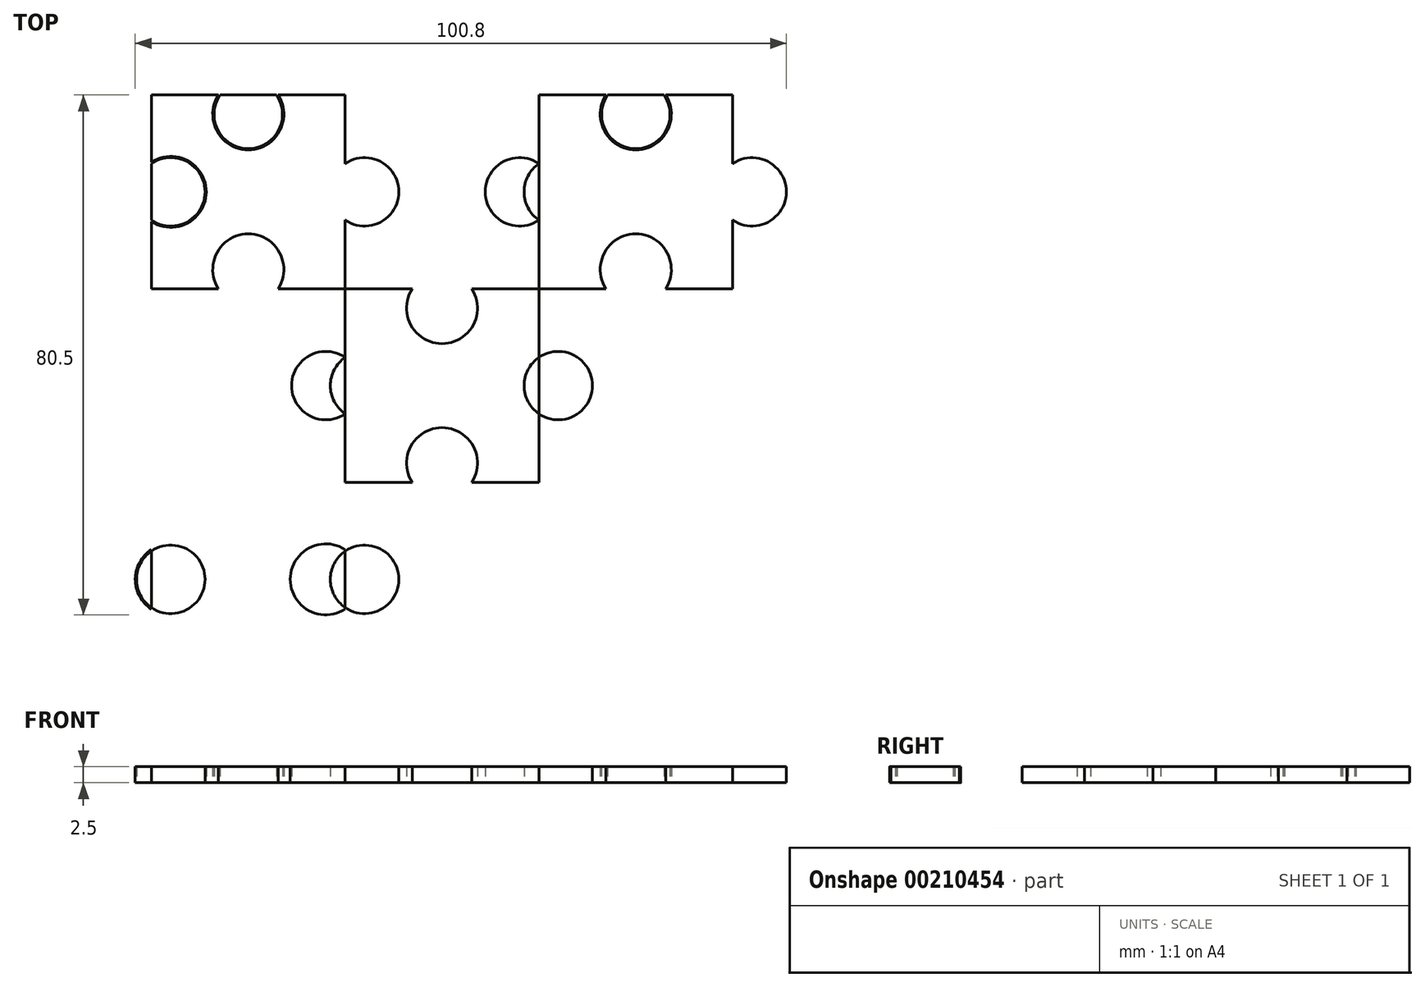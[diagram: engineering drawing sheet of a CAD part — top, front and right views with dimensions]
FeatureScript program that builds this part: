
annotation { "Feature Type Name" : "Feature", "Feature Type Description" : "" }
export const myFeature = defineFeature(function(context is Context, id is Id, definition is map)
    precondition{}
    {
        {
            var Q0;
            Q0=qCreatedBy(makeId("Top.planeOp"),FACE);
            var sketch = newSketch(context, id + "F0", { "sketchPlane" : qUnion([Q0])});
            skLineSegment(sketch, "E0.bottom", {"start": v(15, 15) * mm, "end": v(-15, 15) * mm});
            skLineSegment(sketch, "E0.top", {"start": v(15, -15) * mm, "end": v(-15, -15) * mm});
            skLineSegment(sketch, "E0.left", {"start": v(15, 15) * mm, "end": v(15, -15) * mm});
            skLineSegment(sketch, "E0.right", {"start": v(-15, 15) * mm, "end": v(-15, -15) * mm});
            skPoint(sketch, "E0.middle", {"position": v(0, 0) * mm});
            skPoint(sketch, "E1", {"position": v(0, 15) * mm});
            skPoint(sketch, "E2", {"position": v(-15, 0) * mm});
            skPoint(sketch, "E3", {"position": v(0, -15) * mm});
            skLineSegment(sketch, "E4", {"start": v(-15, 12) * mm, "end": v(15, 12) * mm, "construction": true});
            skCircle(sketch, "E5", {"center": v(0, 12) * mm, "radius": 5.5 * mm});
            skLineSegment(sketch, "E6", {"start": v(-15, 0) * mm, "end": v(15, 0) * mm, "construction": true});
            skCircle(sketch, "E7", {"center": v(0, -12) * mm, "radius": 5.5 * mm});
            skLineSegment(sketch, "E8", {"start": v(-12, 15) * mm, "end": v(-12, -15) * mm, "construction": true});
            skCircle(sketch, "E9", {"center": v(-12, 0) * mm, "radius": 5.5 * mm});
            skLineSegment(sketch, "E10", {"start": v(0, 15) * mm, "end": v(0, -15) * mm, "construction": true});
            skCircle(sketch, "E11", {"center": v(12, 0) * mm, "radius": 5.5 * mm});
            skCircle(sketch, "E12", {"center": v(-12, 0) * mm, "radius": 5.3 * mm});
            skCircle(sketch, "E13", {"center": v(0, 12) * mm, "radius": 5.3 * mm});
            skCircle(sketch, "E14", {"center": v(12, 0) * mm, "radius": 5.3 * mm});
            skCircle(sketch, "E15", {"center": v(0, -12) * mm, "radius": 5.3 * mm});
            skCircle(sketch, "E16.0.1.0", {"center": v(0, -42) * mm, "radius": 5.5 * mm});
            skCircle(sketch, "E16.0.1.1", {"center": v(-12, -30) * mm, "radius": 5.5 * mm});
            skCircle(sketch, "E16.0.1.2", {"center": v(12, -30) * mm, "radius": 5.5 * mm});
            skCircle(sketch, "E16.0.1.3", {"center": v(12, -30) * mm, "radius": 5.3 * mm});
            skLineSegment(sketch, "E16.0.1.4", {"start": v(-12, -15) * mm, "end": v(-12, -45) * mm, "construction": true});
            skPoint(sketch, "E16.0.1.5", {"position": v(0, -45) * mm});
            skLineSegment(sketch, "E16.0.1.6", {"start": v(15, -45) * mm, "end": v(-15, -45) * mm});
            skLineSegment(sketch, "E16.0.1.7", {"start": v(0, -15) * mm, "end": v(0, -45) * mm, "construction": true});
            skCircle(sketch, "E16.0.1.9", {"center": v(0, -42) * mm, "radius": 5.3 * mm});
            skLineSegment(sketch, "E16.0.1.10", {"start": v(15, -15) * mm, "end": v(15, -45) * mm});
            skLineSegment(sketch, "E16.0.1.11", {"start": v(-15, -15) * mm, "end": v(-15, -45) * mm});
            skCircle(sketch, "E16.0.1.12", {"center": v(-12, -30) * mm, "radius": 5.3 * mm});
            skPoint(sketch, "E16.0.1.13", {"position": v(-15, -30) * mm});
            skLineSegment(sketch, "E16.0.1.14", {"start": v(-15, -18) * mm, "end": v(15, -18) * mm, "construction": true});
            skCircle(sketch, "E16.0.1.16", {"center": v(0, -18) * mm, "radius": 5.5 * mm});
            skPoint(sketch, "E16.0.1.17", {"position": v(0, -30) * mm});
            skLineSegment(sketch, "E16.0.1.18", {"start": v(-15, -30) * mm, "end": v(15, -30) * mm, "construction": true});
            skCircle(sketch, "E16.0.1.19", {"center": v(0, -18) * mm, "radius": 5.3 * mm});
            skCircle(sketch, "E16.1.0.0", {"center": v(30, -12) * mm, "radius": 5.5 * mm});
            skCircle(sketch, "E16.1.0.1", {"center": v(18, 0) * mm, "radius": 5.5 * mm});
            skCircle(sketch, "E16.1.0.2", {"center": v(42, 0) * mm, "radius": 5.5 * mm});
            skCircle(sketch, "E16.1.0.3", {"center": v(42, 0) * mm, "radius": 5.3 * mm});
            skLineSegment(sketch, "E16.1.0.4", {"start": v(18, 15) * mm, "end": v(18, -15) * mm, "construction": true});
            skPoint(sketch, "E16.1.0.5", {"position": v(30, -15) * mm});
            skLineSegment(sketch, "E16.1.0.6", {"start": v(45, -15) * mm, "end": v(15, -15) * mm});
            skLineSegment(sketch, "E16.1.0.7", {"start": v(30, 15) * mm, "end": v(30, -15) * mm, "construction": true});
            skLineSegment(sketch, "E16.1.0.8", {"start": v(45, 15) * mm, "end": v(15, 15) * mm});
            skCircle(sketch, "E16.1.0.9", {"center": v(30, -12) * mm, "radius": 5.3 * mm});
            skLineSegment(sketch, "E16.1.0.10", {"start": v(45, 15) * mm, "end": v(45, -15) * mm});
            skCircle(sketch, "E16.1.0.12", {"center": v(18, 0) * mm, "radius": 5.3 * mm});
            skPoint(sketch, "E16.1.0.13", {"position": v(15, 0) * mm});
            skLineSegment(sketch, "E16.1.0.14", {"start": v(15, 12) * mm, "end": v(45, 12) * mm, "construction": true});
            skPoint(sketch, "E16.1.0.15", {"position": v(30, 15) * mm});
            skCircle(sketch, "E16.1.0.16", {"center": v(30, 12) * mm, "radius": 5.5 * mm});
            skPoint(sketch, "E16.1.0.17", {"position": v(30, 0) * mm});
            skLineSegment(sketch, "E16.1.0.18", {"start": v(15, 0) * mm, "end": v(45, 0) * mm, "construction": true});
            skCircle(sketch, "E16.1.0.19", {"center": v(30, 12) * mm, "radius": 5.3 * mm});
            skCircle(sketch, "E16.1.1.0", {"center": v(30, -42) * mm, "radius": 5.5 * mm});
            skCircle(sketch, "E16.1.1.1", {"center": v(18, -30) * mm, "radius": 5.5 * mm});
            skCircle(sketch, "E16.1.1.2", {"center": v(42, -30) * mm, "radius": 5.5 * mm});
            skCircle(sketch, "E16.1.1.3", {"center": v(42, -30) * mm, "radius": 5.3 * mm});
            skLineSegment(sketch, "E16.1.1.4", {"start": v(18, -15) * mm, "end": v(18, -45) * mm, "construction": true});
            skPoint(sketch, "E16.1.1.5", {"position": v(30, -45) * mm});
            skLineSegment(sketch, "E16.1.1.6", {"start": v(45, -45) * mm, "end": v(15, -45) * mm});
            skLineSegment(sketch, "E16.1.1.7", {"start": v(30, -15) * mm, "end": v(30, -45) * mm, "construction": true});
            skLineSegment(sketch, "E16.1.1.8", {"start": v(45, -15) * mm, "end": v(15, -15) * mm});
            skCircle(sketch, "E16.1.1.9", {"center": v(30, -42) * mm, "radius": 5.3 * mm});
            skLineSegment(sketch, "E16.1.1.10", {"start": v(45, -15) * mm, "end": v(45, -45) * mm});
            skLineSegment(sketch, "E16.1.1.11", {"start": v(15, -15) * mm, "end": v(15, -45) * mm});
            skCircle(sketch, "E16.1.1.12", {"center": v(18, -30) * mm, "radius": 5.3 * mm});
            skPoint(sketch, "E16.1.1.13", {"position": v(15, -30) * mm});
            skLineSegment(sketch, "E16.1.1.14", {"start": v(15, -18) * mm, "end": v(45, -18) * mm, "construction": true});
            skPoint(sketch, "E16.1.1.15", {"position": v(30, -15) * mm});
            skCircle(sketch, "E16.1.1.16", {"center": v(30, -18) * mm, "radius": 5.5 * mm});
            skPoint(sketch, "E16.1.1.17", {"position": v(30, -30) * mm});
            skLineSegment(sketch, "E16.1.1.18", {"start": v(15, -30) * mm, "end": v(45, -30) * mm, "construction": true});
            skCircle(sketch, "E16.1.1.19", {"center": v(30, -18) * mm, "radius": 5.3 * mm});
            skCircle(sketch, "E16.2.0.0", {"center": v(60, -12) * mm, "radius": 5.5 * mm});
            skCircle(sketch, "E16.2.0.1", {"center": v(48, 0) * mm, "radius": 5.5 * mm});
            skCircle(sketch, "E16.2.0.2", {"center": v(72, 0) * mm, "radius": 5.5 * mm});
            skCircle(sketch, "E16.2.0.3", {"center": v(72, 0) * mm, "radius": 5.3 * mm});
            skLineSegment(sketch, "E16.2.0.4", {"start": v(48, 15) * mm, "end": v(48, -15) * mm, "construction": true});
            skPoint(sketch, "E16.2.0.5", {"position": v(60, -15) * mm});
            skLineSegment(sketch, "E16.2.0.6", {"start": v(75, -15) * mm, "end": v(45, -15) * mm});
            skLineSegment(sketch, "E16.2.0.7", {"start": v(60, 15) * mm, "end": v(60, -15) * mm, "construction": true});
            skLineSegment(sketch, "E16.2.0.8", {"start": v(75, 15) * mm, "end": v(45, 15) * mm});
            skCircle(sketch, "E16.2.0.9", {"center": v(60, -12) * mm, "radius": 5.3 * mm});
            skLineSegment(sketch, "E16.2.0.10", {"start": v(75, 15) * mm, "end": v(75, -15) * mm});
            skLineSegment(sketch, "E16.2.0.11", {"start": v(45, 15) * mm, "end": v(45, -15) * mm});
            skCircle(sketch, "E16.2.0.12", {"center": v(48, 0) * mm, "radius": 5.3 * mm});
            skPoint(sketch, "E16.2.0.13", {"position": v(45, 0) * mm});
            skLineSegment(sketch, "E16.2.0.14", {"start": v(45, 12) * mm, "end": v(75, 12) * mm, "construction": true});
            skPoint(sketch, "E16.2.0.15", {"position": v(60, 15) * mm});
            skCircle(sketch, "E16.2.0.16", {"center": v(60, 12) * mm, "radius": 5.5 * mm});
            skPoint(sketch, "E16.2.0.17", {"position": v(60, 0) * mm});
            skLineSegment(sketch, "E16.2.0.18", {"start": v(45, 0) * mm, "end": v(75, 0) * mm, "construction": true});
            skCircle(sketch, "E16.2.0.19", {"center": v(60, 12) * mm, "radius": 5.3 * mm});
            skCircle(sketch, "E16.2.1.0", {"center": v(60, -42) * mm, "radius": 5.5 * mm});
            skCircle(sketch, "E16.2.1.1", {"center": v(48, -30) * mm, "radius": 5.5 * mm});
            skCircle(sketch, "E16.2.1.2", {"center": v(72, -30) * mm, "radius": 5.5 * mm});
            skCircle(sketch, "E16.2.1.3", {"center": v(72, -30) * mm, "radius": 5.3 * mm});
            skLineSegment(sketch, "E16.2.1.4", {"start": v(48, -15) * mm, "end": v(48, -45) * mm, "construction": true});
            skPoint(sketch, "E16.2.1.5", {"position": v(60, -45) * mm});
            skLineSegment(sketch, "E16.2.1.6", {"start": v(75, -45) * mm, "end": v(45, -45) * mm});
            skLineSegment(sketch, "E16.2.1.7", {"start": v(60, -15) * mm, "end": v(60, -45) * mm, "construction": true});
            skLineSegment(sketch, "E16.2.1.8", {"start": v(75, -15) * mm, "end": v(45, -15) * mm});
            skCircle(sketch, "E16.2.1.9", {"center": v(60, -42) * mm, "radius": 5.3 * mm});
            skLineSegment(sketch, "E16.2.1.10", {"start": v(75, -15) * mm, "end": v(75, -45) * mm});
            skLineSegment(sketch, "E16.2.1.11", {"start": v(45, -15) * mm, "end": v(45, -45) * mm});
            skCircle(sketch, "E16.2.1.12", {"center": v(48, -30) * mm, "radius": 5.3 * mm});
            skPoint(sketch, "E16.2.1.13", {"position": v(45, -30) * mm});
            skLineSegment(sketch, "E16.2.1.14", {"start": v(45, -18) * mm, "end": v(75, -18) * mm, "construction": true});
            skPoint(sketch, "E16.2.1.15", {"position": v(60, -15) * mm});
            skCircle(sketch, "E16.2.1.16", {"center": v(60, -18) * mm, "radius": 5.5 * mm});
            skPoint(sketch, "E16.2.1.17", {"position": v(60, -30) * mm});
            skLineSegment(sketch, "E16.2.1.18", {"start": v(45, -30) * mm, "end": v(75, -30) * mm, "construction": true});
            skCircle(sketch, "E16.2.1.19", {"center": v(60, -18) * mm, "radius": 5.3 * mm});
            skLineSegment(sketch, "E16.direction1", {"start": v(-15, -15) * mm, "end": v(15, -15) * mm, "construction": true});
            skLineSegment(sketch, "E16.direction2", {"start": v(-15, -15) * mm, "end": v(-15, -45) * mm, "construction": true});
            skCircle(sketch, "E17.0.0.2", {"center": v(0, -72) * mm, "radius": 5.5 * mm});
            skCircle(sketch, "E17.2.0.2", {"center": v(-12, -60) * mm, "radius": 5.5 * mm});
            skCircle(sketch, "E17.4.0.2", {"center": v(12, -60) * mm, "radius": 5.5 * mm});
            skCircle(sketch, "E17.6.0.2", {"center": v(12, -60) * mm, "radius": 5.3 * mm});
            skLineSegment(sketch, "E17.8.0.2", {"start": v(-12, -45) * mm, "end": v(-12, -75) * mm, "construction": true});
            skPoint(sketch, "E17.11.0.2", {"position": v(0, -75) * mm});
            skLineSegment(sketch, "E17.12.0.2", {"start": v(15, -75) * mm, "end": v(-15, -75) * mm});
            skLineSegment(sketch, "E17.15.0.2", {"start": v(0, -45) * mm, "end": v(0, -75) * mm, "construction": true});
            skCircle(sketch, "E17.21.0.2", {"center": v(0, -72) * mm, "radius": 5.3 * mm});
            skLineSegment(sketch, "E17.23.0.2", {"start": v(15, -45) * mm, "end": v(15, -75) * mm});
            skLineSegment(sketch, "E17.26.0.2", {"start": v(-15, -45) * mm, "end": v(-15, -75) * mm});
            skCircle(sketch, "E17.29.0.2", {"center": v(-12, -60) * mm, "radius": 5.3 * mm});
            skPoint(sketch, "E17.31.0.2", {"position": v(-15, -60) * mm});
            skLineSegment(sketch, "E17.32.0.2", {"start": v(-15, -48) * mm, "end": v(15, -48) * mm, "construction": true});
            skCircle(sketch, "E17.36.0.2", {"center": v(0, -48) * mm, "radius": 5.5 * mm});
            skPoint(sketch, "E17.38.0.2", {"position": v(0, -60) * mm});
            skLineSegment(sketch, "E17.39.0.2", {"start": v(-15, -60) * mm, "end": v(15, -60) * mm, "construction": true});
            skCircle(sketch, "E17.42.0.2", {"center": v(0, -48) * mm, "radius": 5.3 * mm});
            skCircle(sketch, "E17.0.1.2", {"center": v(30, -72) * mm, "radius": 5.5 * mm});
            skCircle(sketch, "E17.2.1.2", {"center": v(18, -60) * mm, "radius": 5.5 * mm});
            skCircle(sketch, "E17.4.1.2", {"center": v(42, -60) * mm, "radius": 5.5 * mm});
            skCircle(sketch, "E17.6.1.2", {"center": v(42, -60) * mm, "radius": 5.3 * mm});
            skLineSegment(sketch, "E17.8.1.2", {"start": v(18, -45) * mm, "end": v(18, -75) * mm, "construction": true});
            skPoint(sketch, "E17.11.1.2", {"position": v(30, -75) * mm});
            skLineSegment(sketch, "E17.12.1.2", {"start": v(45, -75) * mm, "end": v(15, -75) * mm});
            skLineSegment(sketch, "E17.15.1.2", {"start": v(30, -45) * mm, "end": v(30, -75) * mm, "construction": true});
            skCircle(sketch, "E17.21.1.2", {"center": v(30, -72) * mm, "radius": 5.3 * mm});
            skLineSegment(sketch, "E17.23.1.2", {"start": v(45, -45) * mm, "end": v(45, -75) * mm});
            skLineSegment(sketch, "E17.26.1.2", {"start": v(15, -45) * mm, "end": v(15, -75) * mm});
            skCircle(sketch, "E17.29.1.2", {"center": v(18, -60) * mm, "radius": 5.3 * mm});
            skPoint(sketch, "E17.31.1.2", {"position": v(15, -60) * mm});
            skLineSegment(sketch, "E17.32.1.2", {"start": v(15, -48) * mm, "end": v(45, -48) * mm, "construction": true});
            skCircle(sketch, "E17.36.1.2", {"center": v(30, -48) * mm, "radius": 5.5 * mm});
            skPoint(sketch, "E17.38.1.2", {"position": v(30, -60) * mm});
            skLineSegment(sketch, "E17.39.1.2", {"start": v(15, -60) * mm, "end": v(45, -60) * mm, "construction": true});
            skCircle(sketch, "E17.42.1.2", {"center": v(30, -48) * mm, "radius": 5.3 * mm});
            skCircle(sketch, "E17.0.2.2", {"center": v(60, -72) * mm, "radius": 5.5 * mm});
            skCircle(sketch, "E17.2.2.2", {"center": v(48, -60) * mm, "radius": 5.5 * mm});
            skCircle(sketch, "E17.4.2.2", {"center": v(72, -60) * mm, "radius": 5.5 * mm});
            skCircle(sketch, "E17.6.2.2", {"center": v(72, -60) * mm, "radius": 5.3 * mm});
            skLineSegment(sketch, "E17.8.2.2", {"start": v(48, -45) * mm, "end": v(48, -75) * mm, "construction": true});
            skPoint(sketch, "E17.11.2.2", {"position": v(60, -75) * mm});
            skLineSegment(sketch, "E17.12.2.2", {"start": v(75, -75) * mm, "end": v(45, -75) * mm});
            skLineSegment(sketch, "E17.15.2.2", {"start": v(60, -45) * mm, "end": v(60, -75) * mm, "construction": true});
            skCircle(sketch, "E17.21.2.2", {"center": v(60, -72) * mm, "radius": 5.3 * mm});
            skLineSegment(sketch, "E17.23.2.2", {"start": v(75, -45) * mm, "end": v(75, -75) * mm});
            skLineSegment(sketch, "E17.26.2.2", {"start": v(45, -45) * mm, "end": v(45, -75) * mm});
            skCircle(sketch, "E17.29.2.2", {"center": v(48, -60) * mm, "radius": 5.3 * mm});
            skPoint(sketch, "E17.31.2.2", {"position": v(45, -60) * mm});
            skLineSegment(sketch, "E17.32.2.2", {"start": v(45, -48) * mm, "end": v(75, -48) * mm, "construction": true});
            skCircle(sketch, "E17.36.2.2", {"center": v(60, -48) * mm, "radius": 5.5 * mm});
            skPoint(sketch, "E17.38.2.2", {"position": v(60, -60) * mm});
            skLineSegment(sketch, "E17.39.2.2", {"start": v(45, -60) * mm, "end": v(75, -60) * mm, "construction": true});
            skCircle(sketch, "E17.42.2.2", {"center": v(60, -48) * mm, "radius": 5.3 * mm});
            skCircle(sketch, "E18.0.3.0", {"center": v(90, -12) * mm, "radius": 5.5 * mm});
            skCircle(sketch, "E18.2.3.0", {"center": v(78, 0) * mm, "radius": 5.5 * mm});
            skCircle(sketch, "E18.4.3.0", {"center": v(102, 0) * mm, "radius": 5.5 * mm});
            skCircle(sketch, "E18.6.3.0", {"center": v(102, 0) * mm, "radius": 5.3 * mm});
            skLineSegment(sketch, "E18.8.3.0", {"start": v(78, 15) * mm, "end": v(78, -15) * mm, "construction": true});
            skPoint(sketch, "E18.11.3.0", {"position": v(90, -15) * mm});
            skLineSegment(sketch, "E18.12.3.0", {"start": v(105, -15) * mm, "end": v(75, -15) * mm});
            skLineSegment(sketch, "E18.15.3.0", {"start": v(90, 15) * mm, "end": v(90, -15) * mm, "construction": true});
            skLineSegment(sketch, "E18.18.3.0", {"start": v(105, 15) * mm, "end": v(75, 15) * mm});
            skCircle(sketch, "E18.21.3.0", {"center": v(90, -12) * mm, "radius": 5.3 * mm});
            skLineSegment(sketch, "E18.23.3.0", {"start": v(105, 15) * mm, "end": v(105, -15) * mm});
            skCircle(sketch, "E18.29.3.0", {"center": v(78, 0) * mm, "radius": 5.3 * mm});
            skPoint(sketch, "E18.31.3.0", {"position": v(75, 0) * mm});
            skLineSegment(sketch, "E18.32.3.0", {"start": v(75, 12) * mm, "end": v(105, 12) * mm, "construction": true});
            skPoint(sketch, "E18.35.3.0", {"position": v(90, 15) * mm});
            skCircle(sketch, "E18.36.3.0", {"center": v(90, 12) * mm, "radius": 5.5 * mm});
            skPoint(sketch, "E18.38.3.0", {"position": v(90, 0) * mm});
            skLineSegment(sketch, "E18.39.3.0", {"start": v(75, 0) * mm, "end": v(105, 0) * mm, "construction": true});
            skCircle(sketch, "E18.42.3.0", {"center": v(90, 12) * mm, "radius": 5.3 * mm});
            skCircle(sketch, "E18.0.3.1", {"center": v(90, -42) * mm, "radius": 5.5 * mm});
            skCircle(sketch, "E18.2.3.1", {"center": v(78, -30) * mm, "radius": 5.5 * mm});
            skCircle(sketch, "E18.4.3.1", {"center": v(102, -30) * mm, "radius": 5.5 * mm});
            skCircle(sketch, "E18.6.3.1", {"center": v(102, -30) * mm, "radius": 5.3 * mm});
            skLineSegment(sketch, "E18.8.3.1", {"start": v(78, -15) * mm, "end": v(78, -45) * mm, "construction": true});
            skPoint(sketch, "E18.11.3.1", {"position": v(90, -45) * mm});
            skLineSegment(sketch, "E18.12.3.1", {"start": v(105, -45) * mm, "end": v(75, -45) * mm});
            skLineSegment(sketch, "E18.15.3.1", {"start": v(90, -15) * mm, "end": v(90, -45) * mm, "construction": true});
            skLineSegment(sketch, "E18.18.3.1", {"start": v(105, -15) * mm, "end": v(75, -15) * mm});
            skCircle(sketch, "E18.21.3.1", {"center": v(90, -42) * mm, "radius": 5.3 * mm});
            skLineSegment(sketch, "E18.23.3.1", {"start": v(105, -15) * mm, "end": v(105, -45) * mm});
            skCircle(sketch, "E18.29.3.1", {"center": v(78, -30) * mm, "radius": 5.3 * mm});
            skPoint(sketch, "E18.31.3.1", {"position": v(75, -30) * mm});
            skLineSegment(sketch, "E18.32.3.1", {"start": v(75, -18) * mm, "end": v(105, -18) * mm, "construction": true});
            skPoint(sketch, "E18.35.3.1", {"position": v(90, -15) * mm});
            skCircle(sketch, "E18.36.3.1", {"center": v(90, -18) * mm, "radius": 5.5 * mm});
            skPoint(sketch, "E18.38.3.1", {"position": v(90, -30) * mm});
            skLineSegment(sketch, "E18.39.3.1", {"start": v(75, -30) * mm, "end": v(105, -30) * mm, "construction": true});
            skCircle(sketch, "E18.42.3.1", {"center": v(90, -18) * mm, "radius": 5.3 * mm});
            skCircle(sketch, "E18.0.3.2", {"center": v(90, -72) * mm, "radius": 5.5 * mm});
            skCircle(sketch, "E18.2.3.2", {"center": v(78, -60) * mm, "radius": 5.5 * mm});
            skCircle(sketch, "E18.4.3.2", {"center": v(102, -60) * mm, "radius": 5.5 * mm});
            skCircle(sketch, "E18.6.3.2", {"center": v(102, -60) * mm, "radius": 5.3 * mm});
            skLineSegment(sketch, "E18.8.3.2", {"start": v(78, -45) * mm, "end": v(78, -75) * mm, "construction": true});
            skPoint(sketch, "E18.11.3.2", {"position": v(90, -75) * mm});
            skLineSegment(sketch, "E18.12.3.2", {"start": v(105, -75) * mm, "end": v(75, -75) * mm});
            skLineSegment(sketch, "E18.15.3.2", {"start": v(90, -45) * mm, "end": v(90, -75) * mm, "construction": true});
            skLineSegment(sketch, "E18.18.3.2", {"start": v(105, -45) * mm, "end": v(75, -45) * mm});
            skCircle(sketch, "E18.21.3.2", {"center": v(90, -72) * mm, "radius": 5.3 * mm});
            skLineSegment(sketch, "E18.23.3.2", {"start": v(105, -45) * mm, "end": v(105, -75) * mm});
            skCircle(sketch, "E18.29.3.2", {"center": v(78, -60) * mm, "radius": 5.3 * mm});
            skPoint(sketch, "E18.31.3.2", {"position": v(75, -60) * mm});
            skLineSegment(sketch, "E18.32.3.2", {"start": v(75, -48) * mm, "end": v(105, -48) * mm, "construction": true});
            skPoint(sketch, "E18.35.3.2", {"position": v(90, -45) * mm});
            skCircle(sketch, "E18.36.3.2", {"center": v(90, -48) * mm, "radius": 5.5 * mm});
            skPoint(sketch, "E18.38.3.2", {"position": v(90, -60) * mm});
            skLineSegment(sketch, "E18.39.3.2", {"start": v(75, -60) * mm, "end": v(105, -60) * mm, "construction": true});
            skCircle(sketch, "E18.42.3.2", {"center": v(90, -48) * mm, "radius": 5.3 * mm});
            skSolve(sketch);
        }
        {
            var Q0;
            {var subQ1=sQuery(id+"F0.wireOp",EDGE,"E0.right");var subQ13=sQuery(id+"F0.wireOp",EDGE,"E0.bottom");var subQ14=makeQuery(id+"F0.imprint","INTERSECT",VERTEX,{"derivedFrom":[subQ13,subQ1]});Q0=makeQuery(id+"F0.imprint","IMPRINT",FACE,{"disambiguationData":[TD([[makeQuery(id+"F0.imprint","IMPRINT",EDGE,{"disambiguationData":[TD([[subQ14,1.0]])],"derivedFrom":subQ13}),1.0]])]});}
            var Q1;
            {var subQ0=sQuery(id+"F0.wireOp",EDGE,"E5");var subQ1=sQuery(id+"F0.wireOp",EDGE,"E0.bottom");var subQ2=makeQuery(id+"F0.imprint","INTERSECT",VERTEX,{"disambiguationData":[OD(0.0)],"derivedFrom":[subQ1,subQ0]});Q1=makeQuery(id+"F0.imprint","IMPRINT",FACE,{"disambiguationData":[TD([[makeQuery(id+"F0.imprint","IMPRINT",EDGE,{"disambiguationData":[TD([[subQ2,-1.0]])],"derivedFrom":subQ1}),1.0]])]});}
            var Q2;
            {var subQ0=sQuery(id+"F0.wireOp",EDGE,"E16.1.0.12");var subQ1=sQuery(id+"F0.wireOp",EDGE,"E11");var subQ2=makeQuery(id+"F0.imprint","INTERSECT",VERTEX,{"disambiguationData":[OD(0.0)],"derivedFrom":[subQ1,subQ0]});Q2=makeQuery(id+"F0.imprint","IMPRINT",FACE,{"disambiguationData":[TD([[makeQuery(id+"F0.imprint","IMPRINT",EDGE,{"disambiguationData":[TD([[subQ2,1.0]])],"derivedFrom":subQ1}),1.0]])]});}
            var Q3;
            {var subQ0=sQuery(id+"F0.wireOp",EDGE,"E12");var subQ1=sQuery(id+"F0.wireOp",EDGE,"E0.right");var subQ2=makeQuery(id+"F0.imprint","INTERSECT",VERTEX,{"disambiguationData":[OD(0.0)],"derivedFrom":[subQ1,subQ0]});Q3=makeQuery(id+"F0.imprint","IMPRINT",FACE,{"disambiguationData":[TD([[makeQuery(id+"F0.imprint","IMPRINT",EDGE,{"disambiguationData":[TD([[subQ2,-1.0]])],"derivedFrom":subQ1}),1.0]])]});}
            var Q4;
            {var subQ0=sQuery(id+"F0.wireOp",EDGE,"E13");var subQ1=sQuery(id+"F0.wireOp",EDGE,"E0.bottom");var subQ2=makeQuery(id+"F0.imprint","INTERSECT",VERTEX,{"disambiguationData":[OD(0.0)],"derivedFrom":[subQ1,subQ0]});Q4=makeQuery(id+"F0.imprint","IMPRINT",FACE,{"disambiguationData":[TD([[makeQuery(id+"F0.imprint","IMPRINT",EDGE,{"disambiguationData":[TD([[subQ2,-1.0]])],"derivedFrom":subQ1}),1.0]])]});}
            var Q5;
            {var subQ0=sQuery(id+"F0.wireOp",EDGE,"E16.1.0.1");var subQ1=sQuery(id+"F0.wireOp",EDGE,"E14");var subQ2=makeQuery(id+"F0.imprint","INTERSECT",VERTEX,{"disambiguationData":[OD(0.0)],"derivedFrom":[subQ1,subQ0]});Q5=makeQuery(id+"F0.imprint","IMPRINT",FACE,{"disambiguationData":[TD([[makeQuery(id+"F0.imprint","IMPRINT",EDGE,{"disambiguationData":[TD([[subQ2,-1.0]])],"derivedFrom":subQ1}),1.0]])]});}
            var Q6;
            {var subQ0=sQuery(id+"F0.wireOp",EDGE,"E16.1.0.12");var subQ1=sQuery(id+"F0.wireOp",EDGE,"E0.left");var subQ2=sQuery(id+"F0.wireOp",EDGE,"E14");var subQ3=makeQuery(id+"F0.imprint","INTERSECT",VERTEX,{"disambiguationData":[OD(0.0)],"derivedFrom":[subQ2,subQ1,subQ0]});Q6=makeQuery(id+"F0.imprint","IMPRINT",FACE,{"disambiguationData":[TD([[makeQuery(id+"F0.imprint","IMPRINT",EDGE,{"disambiguationData":[TD([[subQ3,-1.0]])],"derivedFrom":subQ1}),-1.0]])]});}
            var Q7;
            {var subQ0=sQuery(id+"F0.wireOp",EDGE,"E16.1.0.12");var subQ1=sQuery(id+"F0.wireOp",EDGE,"E0.left");var subQ2=sQuery(id+"F0.wireOp",EDGE,"E14");var subQ3=makeQuery(id+"F0.imprint","INTERSECT",VERTEX,{"disambiguationData":[OD(0.0)],"derivedFrom":[subQ2,subQ1,subQ0]});Q7=makeQuery(id+"F0.imprint","IMPRINT",FACE,{"disambiguationData":[TD([[makeQuery(id+"F0.imprint","IMPRINT",EDGE,{"disambiguationData":[TD([[subQ3,1.0]])],"derivedFrom":subQ2}),1.0]])]});}
            var Q8;
            {var subQ0=sQuery(id+"F0.wireOp",EDGE,"E16.1.0.12");var subQ1=sQuery(id+"F0.wireOp",EDGE,"E11");var subQ2=makeQuery(id+"F0.imprint","INTERSECT",VERTEX,{"disambiguationData":[OD(0.0)],"derivedFrom":[subQ1,subQ0]});Q8=makeQuery(id+"F0.imprint","IMPRINT",FACE,{"disambiguationData":[TD([[makeQuery(id+"F0.imprint","IMPRINT",EDGE,{"disambiguationData":[TD([[subQ2,1.0]])],"derivedFrom":subQ1}),-1.0]])]});}
            var Q9;
            {var subQ0=sQuery(id+"F0.wireOp",EDGE,"E16.1.0.1");var subQ1=sQuery(id+"F0.wireOp",EDGE,"E14");var subQ2=makeQuery(id+"F0.imprint","INTERSECT",VERTEX,{"disambiguationData":[OD(0.0)],"derivedFrom":[subQ1,subQ0]});Q9=makeQuery(id+"F0.imprint","IMPRINT",FACE,{"disambiguationData":[TD([[makeQuery(id+"F0.imprint","IMPRINT",EDGE,{"disambiguationData":[TD([[subQ2,-1.0]])],"derivedFrom":subQ0}),1.0]])]});}
            var Q10;
            {var subQ0=sQuery(id+"F0.wireOp",EDGE,"E9");var subQ1=sQuery(id+"F0.wireOp",EDGE,"E0.right");var subQ2=makeQuery(id+"F0.imprint","INTERSECT",VERTEX,{"disambiguationData":[OD(0.0)],"derivedFrom":[subQ1,subQ0]});Q10=makeQuery(id+"F0.imprint","IMPRINT",FACE,{"disambiguationData":[TD([[makeQuery(id+"F0.imprint","IMPRINT",EDGE,{"disambiguationData":[TD([[subQ2,-1.0]])],"derivedFrom":subQ1}),1.0]])]});}
            var Q11;
            {var subQ1=sQuery(id+"F0.wireOp",EDGE,"E16.1.0.1");var subQ5=sQuery(id+"F0.wireOp",EDGE,"E14");var subQ6=makeQuery(id+"F0.imprint","INTERSECT",VERTEX,{"disambiguationData":[OD(0.0)],"derivedFrom":[subQ5,subQ1]});Q11=makeQuery(id+"F0.imprint","IMPRINT",FACE,{"disambiguationData":[TD([[makeQuery(id+"F0.imprint","IMPRINT",EDGE,{"disambiguationData":[TD([[subQ6,-1.0]])],"derivedFrom":subQ5}),-1.0]])]});}
            var Q12;
            {var subQ0=sQuery(id+"F0.wireOp",EDGE,"E16.1.0.1");var subQ1=sQuery(id+"F0.wireOp",EDGE,"E14");var subQ2=makeQuery(id+"F0.imprint","INTERSECT",VERTEX,{"disambiguationData":[OD(0.0)],"derivedFrom":[subQ1,subQ0]});Q12=makeQuery(id+"F0.imprint","IMPRINT",FACE,{"disambiguationData":[TD([[makeQuery(id+"F0.imprint","IMPRINT",EDGE,{"disambiguationData":[TD([[subQ2,1.0]])],"derivedFrom":subQ1}),-1.0]])]});}
            var Q13;
            {var subQ0=sQuery(id+"F0.wireOp",EDGE,"E16.1.0.1");var subQ1=sQuery(id+"F0.wireOp",EDGE,"E14");var subQ2=makeQuery(id+"F0.imprint","INTERSECT",VERTEX,{"disambiguationData":[OD(1.0)],"derivedFrom":[subQ1,subQ0]});Q13=makeQuery(id+"F0.imprint","IMPRINT",FACE,{"disambiguationData":[TD([[makeQuery(id+"F0.imprint","IMPRINT",EDGE,{"disambiguationData":[TD([[subQ2,-1.0]])],"derivedFrom":subQ1}),-1.0]])]});}
            extrude(context, id + "F1", {"entities" : qUnion([Q0, Q1, Q2, Q3, Q4, Q5, Q6, Q7, Q8, Q9, Q10, Q11, Q12, Q13]), "depth" : 2.5 * mm});
        }
        {
            var Q0;
            {var subQ1=sQuery(id+"F0.wireOp",EDGE,"adf34985-a7f9-4340-8066-421a328eff77.28.0.2");var subQ17=sQuery(id+"F0.wireOp",EDGE,"adf34985-a7f9-4340-8066-421a328eff77.2.0.2");var subQ19=makeQuery(id+"F0.imprint","INTERSECT",VERTEX,{"disambiguationData":[OD(0.0)],"derivedFrom":[subQ17,subQ1]});Q0=makeQuery(id+"F0.imprint","IMPRINT",FACE,{"disambiguationData":[TD([[makeQuery(id+"F0.imprint","IMPRINT",EDGE,{"disambiguationData":[TD([[subQ19,1.0]])],"derivedFrom":subQ17}),-1.0]])]});}
            var Q1;
            {var subQ0=sQuery(id+"F0.wireOp",EDGE,"adf34985-a7f9-4340-8066-421a328eff77.28.0.2");var subQ1=sQuery(id+"F0.wireOp",EDGE,"adf34985-a7f9-4340-8066-421a328eff77.2.0.2");var subQ2=makeQuery(id+"F0.imprint","INTERSECT",VERTEX,{"disambiguationData":[OD(0.0)],"derivedFrom":[subQ1,subQ0]});Q1=makeQuery(id+"F0.imprint","IMPRINT",FACE,{"disambiguationData":[TD([[makeQuery(id+"F0.imprint","IMPRINT",EDGE,{"disambiguationData":[TD([[subQ2,1.0]])],"derivedFrom":subQ1}),1.0]])]});}
            var Q2;
            {var subQ0=sQuery(id+"F0.wireOp",EDGE,"adf34985-a7f9-4340-8066-421a328eff77.28.1.2");var subQ1=sQuery(id+"F0.wireOp",EDGE,"adf34985-a7f9-4340-8066-421a328eff77.2.1.2");var subQ2=sQuery(id+"F0.wireOp",EDGE,"adf34985-a7f9-4340-8066-421a328eff77.4.0.2");var subQ3=makeQuery(id+"F0.imprint","INTERSECT",VERTEX,{"disambiguationData":[OD(0.0)],"derivedFrom":[subQ2,subQ1,subQ0]});Q2=makeQuery(id+"F0.imprint","IMPRINT",FACE,{"disambiguationData":[TD([[makeQuery(id+"F0.imprint","IMPRINT",EDGE,{"disambiguationData":[TD([[subQ3,-1.0]])],"derivedFrom":subQ2}),1.0]])]});}
            var Q3;
            {var subQ0=sQuery(id+"F0.wireOp",EDGE,"adf34985-a7f9-4340-8066-421a328eff77.28.1.2");var subQ1=sQuery(id+"F0.wireOp",EDGE,"adf34985-a7f9-4340-8066-421a328eff77.2.1.2");var subQ2=sQuery(id+"F0.wireOp",EDGE,"adf34985-a7f9-4340-8066-421a328eff77.4.0.2");var subQ3=makeQuery(id+"F0.imprint","INTERSECT",VERTEX,{"disambiguationData":[OD(0.0)],"derivedFrom":[subQ2,subQ1,subQ0]});Q3=makeQuery(id+"F0.imprint","IMPRINT",FACE,{"disambiguationData":[TD([[makeQuery(id+"F0.imprint","IMPRINT",EDGE,{"disambiguationData":[TD([[subQ3,1.0]])],"derivedFrom":subQ2}),-1.0]])]});}
            var Q4;
            {var subQ0=sQuery(id+"F0.wireOp",EDGE,"adf34985-a7f9-4340-8066-421a328eff77.28.1.2");var subQ1=sQuery(id+"F0.wireOp",EDGE,"adf34985-a7f9-4340-8066-421a328eff77.2.1.2");var subQ2=sQuery(id+"F0.wireOp",EDGE,"adf34985-a7f9-4340-8066-421a328eff77.4.0.2");var subQ3=makeQuery(id+"F0.imprint","INTERSECT",VERTEX,{"disambiguationData":[OD(0.0)],"derivedFrom":[subQ2,subQ1,subQ0]});Q4=makeQuery(id+"F0.imprint","IMPRINT",FACE,{"disambiguationData":[TD([[makeQuery(id+"F0.imprint","IMPRINT",EDGE,{"disambiguationData":[TD([[subQ3,1.0]])],"derivedFrom":subQ2}),1.0]])]});}
            var Q5;
            {var subQ0=sQuery(id+"F0.wireOp",EDGE,"adf34985-a7f9-4340-8066-421a328eff77.28.1.2");var subQ1=sQuery(id+"F0.wireOp",EDGE,"adf34985-a7f9-4340-8066-421a328eff77.2.1.2");var subQ2=sQuery(id+"F0.wireOp",EDGE,"adf34985-a7f9-4340-8066-421a328eff77.4.0.2");var subQ3=makeQuery(id+"F0.imprint","INTERSECT",VERTEX,{"disambiguationData":[OD(0.0)],"derivedFrom":[subQ2,subQ1,subQ0]});Q5=makeQuery(id+"F0.imprint","IMPRINT",FACE,{"disambiguationData":[TD([[makeQuery(id+"F0.imprint","IMPRINT",EDGE,{"disambiguationData":[TD([[subQ3,-1.0]])],"derivedFrom":subQ1}),1.0]])]});}
            var Q6;
            {var subQ0=sQuery(id+"F0.wireOp",EDGE,"E16.2.0.1");var subQ1=sQuery(id+"F0.wireOp",EDGE,"E16.1.0.3");var subQ2=makeQuery(id+"F0.imprint","INTERSECT",VERTEX,{"disambiguationData":[OD(0.0)],"derivedFrom":[subQ1,subQ0]});Q6=makeQuery(id+"F0.imprint","IMPRINT",FACE,{"disambiguationData":[TD([[makeQuery(id+"F0.imprint","IMPRINT",EDGE,{"disambiguationData":[TD([[subQ2,-1.0]])],"derivedFrom":subQ1}),1.0]])]});}
            var Q7;
            {var subQ0=sQuery(id+"F0.wireOp",EDGE,"E16.2.0.12");var subQ1=sQuery(id+"F0.wireOp",EDGE,"E16.2.0.11");var subQ2=sQuery(id+"F0.wireOp",EDGE,"E16.1.0.3");var subQ3=makeQuery(id+"F0.imprint","INTERSECT",VERTEX,{"disambiguationData":[OD(0.0)],"derivedFrom":[subQ2,subQ1,subQ0]});Q7=makeQuery(id+"F0.imprint","IMPRINT",FACE,{"disambiguationData":[TD([[makeQuery(id+"F0.imprint","IMPRINT",EDGE,{"disambiguationData":[TD([[subQ3,-1.0]])],"derivedFrom":subQ1}),-1.0]])]});}
            var Q8;
            {var subQ0=sQuery(id+"F0.wireOp",EDGE,"E16.2.0.1");var subQ1=sQuery(id+"F0.wireOp",EDGE,"E16.1.0.3");var subQ2=makeQuery(id+"F0.imprint","INTERSECT",VERTEX,{"disambiguationData":[OD(0.0)],"derivedFrom":[subQ1,subQ0]});Q8=makeQuery(id+"F0.imprint","IMPRINT",FACE,{"disambiguationData":[TD([[makeQuery(id+"F0.imprint","IMPRINT",EDGE,{"disambiguationData":[TD([[subQ2,-1.0]])],"derivedFrom":subQ0}),1.0]])]});}
            var Q9;
            {var subQ0=sQuery(id+"F0.wireOp",EDGE,"E16.2.0.12");var subQ1=sQuery(id+"F0.wireOp",EDGE,"E16.2.0.11");var subQ2=sQuery(id+"F0.wireOp",EDGE,"E16.1.0.3");var subQ3=makeQuery(id+"F0.imprint","INTERSECT",VERTEX,{"disambiguationData":[OD(0.0)],"derivedFrom":[subQ2,subQ1,subQ0]});Q9=makeQuery(id+"F0.imprint","IMPRINT",FACE,{"disambiguationData":[TD([[makeQuery(id+"F0.imprint","IMPRINT",EDGE,{"disambiguationData":[TD([[subQ3,1.0]])],"derivedFrom":subQ2}),1.0]])]});}
            var Q10;
            {var subQ0=sQuery(id+"F0.wireOp",EDGE,"E16.2.0.12");var subQ1=sQuery(id+"F0.wireOp",EDGE,"E16.1.0.2");var subQ2=makeQuery(id+"F0.imprint","INTERSECT",VERTEX,{"disambiguationData":[OD(0.0)],"derivedFrom":[subQ1,subQ0]});Q10=makeQuery(id+"F0.imprint","IMPRINT",FACE,{"disambiguationData":[TD([[makeQuery(id+"F0.imprint","IMPRINT",EDGE,{"disambiguationData":[TD([[subQ2,1.0]])],"derivedFrom":subQ1}),1.0]])]});}
            var Q11;
            {var subQ0=sQuery(id+"F0.wireOp",EDGE,"E16.2.0.12");var subQ1=sQuery(id+"F0.wireOp",EDGE,"E16.1.0.2");var subQ2=makeQuery(id+"F0.imprint","INTERSECT",VERTEX,{"disambiguationData":[OD(0.0)],"derivedFrom":[subQ1,subQ0]});Q11=makeQuery(id+"F0.imprint","IMPRINT",FACE,{"disambiguationData":[TD([[makeQuery(id+"F0.imprint","IMPRINT",EDGE,{"disambiguationData":[TD([[subQ2,1.0]])],"derivedFrom":subQ1}),-1.0]])]});}
            var Q12;
            {var subQ0=sQuery(id+"F0.wireOp",EDGE,"E16.2.0.12");var subQ1=sQuery(id+"F0.wireOp",EDGE,"E16.1.0.2");var subQ2=makeQuery(id+"F0.imprint","INTERSECT",VERTEX,{"disambiguationData":[OD(0.0)],"derivedFrom":[subQ1,subQ0]});Q12=makeQuery(id+"F0.imprint","IMPRINT",FACE,{"disambiguationData":[TD([[makeQuery(id+"F0.imprint","IMPRINT",EDGE,{"disambiguationData":[TD([[subQ2,1.0]])],"derivedFrom":subQ0}),-1.0]])]});}
            var Q13;
            {var subQ0=sQuery(id+"F0.wireOp",EDGE,"E16.2.0.16");var subQ1=sQuery(id+"F0.wireOp",EDGE,"E16.2.0.8");var subQ2=makeQuery(id+"F0.imprint","INTERSECT",VERTEX,{"disambiguationData":[OD(0.0)],"derivedFrom":[subQ1,subQ0]});Q13=makeQuery(id+"F0.imprint","IMPRINT",FACE,{"disambiguationData":[TD([[makeQuery(id+"F0.imprint","IMPRINT",EDGE,{"disambiguationData":[TD([[subQ2,1.0]])],"derivedFrom":subQ0}),-1.0]])]});}
            var Q14;
            {var subQ0=sQuery(id+"F0.wireOp",EDGE,"E16.2.0.12");var subQ1=sQuery(id+"F0.wireOp",EDGE,"E16.1.0.2");var subQ2=makeQuery(id+"F0.imprint","INTERSECT",VERTEX,{"disambiguationData":[OD(0.0)],"derivedFrom":[subQ1,subQ0]});Q14=makeQuery(id+"F0.imprint","IMPRINT",FACE,{"disambiguationData":[TD([[makeQuery(id+"F0.imprint","IMPRINT",EDGE,{"disambiguationData":[TD([[subQ2,-1.0]])],"derivedFrom":subQ1}),1.0]])]});}
            var Q15;
            {var subQ0=sQuery(id+"F0.wireOp",EDGE,"E16.2.0.12");var subQ1=sQuery(id+"F0.wireOp",EDGE,"E16.1.0.2");var subQ2=makeQuery(id+"F0.imprint","INTERSECT",VERTEX,{"disambiguationData":[OD(1.0)],"derivedFrom":[subQ1,subQ0]});Q15=makeQuery(id+"F0.imprint","IMPRINT",FACE,{"disambiguationData":[TD([[makeQuery(id+"F0.imprint","IMPRINT",EDGE,{"disambiguationData":[TD([[subQ2,1.0]])],"derivedFrom":subQ1}),1.0]])]});}
            var Q16;
            {var subQ0=sQuery(id+"F0.wireOp",EDGE,"E16.2.0.19");var subQ1=sQuery(id+"F0.wireOp",EDGE,"E16.2.0.8");var subQ2=makeQuery(id+"F0.imprint","INTERSECT",VERTEX,{"disambiguationData":[OD(0.0)],"derivedFrom":[subQ1,subQ0]});Q16=makeQuery(id+"F0.imprint","IMPRINT",FACE,{"disambiguationData":[TD([[makeQuery(id+"F0.imprint","IMPRINT",EDGE,{"disambiguationData":[TD([[subQ2,-1.0]])],"derivedFrom":subQ1}),1.0]])]});}
            var Q17;
            {var subQ0=sQuery(id+"F0.wireOp",EDGE,"E16.2.0.16");var subQ1=sQuery(id+"F0.wireOp",EDGE,"E16.2.0.8");var subQ2=makeQuery(id+"F0.imprint","INTERSECT",VERTEX,{"disambiguationData":[OD(0.0)],"derivedFrom":[subQ1,subQ0]});Q17=makeQuery(id+"F0.imprint","IMPRINT",FACE,{"disambiguationData":[TD([[makeQuery(id+"F0.imprint","IMPRINT",EDGE,{"disambiguationData":[TD([[subQ2,-1.0]])],"derivedFrom":subQ1}),1.0]])]});}
            var Q18;
            {var subQ1=sQuery(id+"F0.wireOp",EDGE,"d4da2bad-68f6-4558-bbe9-c2c7651d414e.2.3.0");var subQ5=sQuery(id+"F0.wireOp",EDGE,"E16.2.0.3");var subQ6=makeQuery(id+"F0.imprint","INTERSECT",VERTEX,{"disambiguationData":[OD(0.0)],"derivedFrom":[subQ5,subQ1]});Q18=makeQuery(id+"F0.imprint","IMPRINT",FACE,{"disambiguationData":[TD([[makeQuery(id+"F0.imprint","IMPRINT",EDGE,{"disambiguationData":[TD([[subQ6,-1.0]])],"derivedFrom":subQ5}),-1.0]])]});}
            var Q19;
            {var subQ0=sQuery(id+"F0.wireOp",EDGE,"d4da2bad-68f6-4558-bbe9-c2c7651d414e.2.3.0");var subQ1=sQuery(id+"F0.wireOp",EDGE,"E16.2.0.3");var subQ2=makeQuery(id+"F0.imprint","INTERSECT",VERTEX,{"disambiguationData":[OD(0.0)],"derivedFrom":[subQ1,subQ0]});Q19=makeQuery(id+"F0.imprint","IMPRINT",FACE,{"disambiguationData":[TD([[makeQuery(id+"F0.imprint","IMPRINT",EDGE,{"disambiguationData":[TD([[subQ2,-1.0]])],"derivedFrom":subQ1}),1.0]])]});}
            var Q20;
            {var subQ0=sQuery(id+"F0.wireOp",EDGE,"d4da2bad-68f6-4558-bbe9-c2c7651d414e.2.3.0");var subQ1=sQuery(id+"F0.wireOp",EDGE,"E16.2.0.3");var subQ2=makeQuery(id+"F0.imprint","INTERSECT",VERTEX,{"disambiguationData":[OD(0.0)],"derivedFrom":[subQ1,subQ0]});Q20=makeQuery(id+"F0.imprint","IMPRINT",FACE,{"disambiguationData":[TD([[makeQuery(id+"F0.imprint","IMPRINT",EDGE,{"disambiguationData":[TD([[subQ2,-1.0]])],"derivedFrom":subQ0}),1.0]])]});}
            var Q21;
            {var subQ0=sQuery(id+"F0.wireOp",EDGE,"d4da2bad-68f6-4558-bbe9-c2c7651d414e.29.3.0");var subQ1=sQuery(id+"F0.wireOp",EDGE,"d4da2bad-68f6-4558-bbe9-c2c7651d414e.26.3.0");var subQ2=sQuery(id+"F0.wireOp",EDGE,"E16.2.0.3");var subQ3=makeQuery(id+"F0.imprint","INTERSECT",VERTEX,{"disambiguationData":[OD(0.0)],"derivedFrom":[subQ2,subQ1,subQ0]});Q21=makeQuery(id+"F0.imprint","IMPRINT",FACE,{"disambiguationData":[TD([[makeQuery(id+"F0.imprint","IMPRINT",EDGE,{"disambiguationData":[TD([[subQ3,-1.0]])],"derivedFrom":subQ1}),-1.0]])]});}
            var Q22;
            {var subQ0=sQuery(id+"F0.wireOp",EDGE,"d4da2bad-68f6-4558-bbe9-c2c7651d414e.29.3.0");var subQ1=sQuery(id+"F0.wireOp",EDGE,"d4da2bad-68f6-4558-bbe9-c2c7651d414e.26.3.0");var subQ2=sQuery(id+"F0.wireOp",EDGE,"E16.2.0.3");var subQ3=makeQuery(id+"F0.imprint","INTERSECT",VERTEX,{"disambiguationData":[OD(0.0)],"derivedFrom":[subQ2,subQ1,subQ0]});Q22=makeQuery(id+"F0.imprint","IMPRINT",FACE,{"disambiguationData":[TD([[makeQuery(id+"F0.imprint","IMPRINT",EDGE,{"disambiguationData":[TD([[subQ3,1.0]])],"derivedFrom":subQ2}),1.0]])]});}
            var Q23;
            {var subQ0=sQuery(id+"F0.wireOp",EDGE,"d4da2bad-68f6-4558-bbe9-c2c7651d414e.29.3.0");var subQ1=sQuery(id+"F0.wireOp",EDGE,"E16.2.0.2");var subQ2=makeQuery(id+"F0.imprint","INTERSECT",VERTEX,{"disambiguationData":[OD(0.0)],"derivedFrom":[subQ1,subQ0]});Q23=makeQuery(id+"F0.imprint","IMPRINT",FACE,{"disambiguationData":[TD([[makeQuery(id+"F0.imprint","IMPRINT",EDGE,{"disambiguationData":[TD([[subQ2,1.0]])],"derivedFrom":subQ1}),1.0]])]});}
            var Q24;
            {var subQ0=sQuery(id+"F0.wireOp",EDGE,"d4da2bad-68f6-4558-bbe9-c2c7651d414e.29.3.0");var subQ1=sQuery(id+"F0.wireOp",EDGE,"E16.2.0.2");var subQ2=makeQuery(id+"F0.imprint","INTERSECT",VERTEX,{"disambiguationData":[OD(0.0)],"derivedFrom":[subQ1,subQ0]});Q24=makeQuery(id+"F0.imprint","IMPRINT",FACE,{"disambiguationData":[TD([[makeQuery(id+"F0.imprint","IMPRINT",EDGE,{"disambiguationData":[TD([[subQ2,1.0]])],"derivedFrom":subQ1}),-1.0]])]});}
            var Q25;
            {var subQ0=sQuery(id+"F0.wireOp",EDGE,"d4da2bad-68f6-4558-bbe9-c2c7651d414e.2.3.0");var subQ1=sQuery(id+"F0.wireOp",EDGE,"E16.2.0.3");var subQ2=makeQuery(id+"F0.imprint","INTERSECT",VERTEX,{"disambiguationData":[OD(1.0)],"derivedFrom":[subQ1,subQ0]});Q25=makeQuery(id+"F0.imprint","IMPRINT",FACE,{"disambiguationData":[TD([[makeQuery(id+"F0.imprint","IMPRINT",EDGE,{"disambiguationData":[TD([[subQ2,-1.0]])],"derivedFrom":subQ1}),-1.0]])]});}
            var Q26;
            {var subQ0=sQuery(id+"F0.wireOp",EDGE,"d4da2bad-68f6-4558-bbe9-c2c7651d414e.2.3.0");var subQ1=sQuery(id+"F0.wireOp",EDGE,"E16.2.0.3");var subQ2=makeQuery(id+"F0.imprint","INTERSECT",VERTEX,{"disambiguationData":[OD(0.0)],"derivedFrom":[subQ1,subQ0]});Q26=makeQuery(id+"F0.imprint","IMPRINT",FACE,{"disambiguationData":[TD([[makeQuery(id+"F0.imprint","IMPRINT",EDGE,{"disambiguationData":[TD([[subQ2,1.0]])],"derivedFrom":subQ1}),-1.0]])]});}
            var Q27;
            {var subQ0=sQuery(id+"F0.wireOp",EDGE,"E18.29.3.0");var subQ1=sQuery(id+"F0.wireOp",EDGE,"E16.2.0.10");var subQ2=sQuery(id+"F0.wireOp",EDGE,"E16.2.0.3");var subQ3=makeQuery(id+"F0.imprint","INTERSECT",VERTEX,{"disambiguationData":[OD(0.0)],"derivedFrom":[subQ2,subQ1,subQ0]});Q27=makeQuery(id+"F0.imprint","IMPRINT",FACE,{"disambiguationData":[TD([[makeQuery(id+"F0.imprint","IMPRINT",EDGE,{"disambiguationData":[TD([[subQ3,1.0]])],"derivedFrom":subQ2}),1.0]])]});}
            var Q28;
            {var subQ0=sQuery(id+"F0.wireOp",EDGE,"E18.29.3.0");var subQ1=sQuery(id+"F0.wireOp",EDGE,"E16.2.0.10");var subQ2=sQuery(id+"F0.wireOp",EDGE,"E16.2.0.3");var subQ3=makeQuery(id+"F0.imprint","INTERSECT",VERTEX,{"disambiguationData":[OD(0.0)],"derivedFrom":[subQ2,subQ1,subQ0]});Q28=makeQuery(id+"F0.imprint","IMPRINT",FACE,{"disambiguationData":[TD([[makeQuery(id+"F0.imprint","IMPRINT",EDGE,{"disambiguationData":[TD([[subQ3,-1.0]])],"derivedFrom":subQ1}),-1.0]])]});}
            extrude(context, id + "F2", {"entities" : qUnion([Q0, Q1, Q2, Q3, Q4, Q5, Q6, Q7, Q8, Q9, Q10, Q11, Q12, Q13, Q14, Q15, Q16, Q17, Q18, Q19, Q20, Q21, Q22, Q23, Q24, Q25, Q26, Q27, Q28]), "depth" : 2.5 * mm});
        }
        {
            var Q0;
            {var subQ0=sQuery(id+"F0.wireOp",EDGE,"0c9ff568-a65c-4a2a-8a0e-bc50d92b607b.28.2.0");var subQ1=sQuery(id+"F0.wireOp",EDGE,"0c9ff568-a65c-4a2a-8a0e-bc50d92b607b.2.2.0");var subQ2=sQuery(id+"F0.wireOp",EDGE,"a8acdf89-7f2b-4dc1-95ab-7df2acf25f29.1.0.2");var subQ3=makeQuery(id+"F0.imprint","INTERSECT",VERTEX,{"disambiguationData":[OD(0.0)],"derivedFrom":[subQ2,subQ1,subQ0]});Q0=makeQuery(id+"F0.imprint","IMPRINT",FACE,{"disambiguationData":[TD([[makeQuery(id+"F0.imprint","IMPRINT",EDGE,{"disambiguationData":[TD([[subQ3,-1.0]])],"derivedFrom":subQ1}),1.0]])]});}
            var Q1;
            {var subQ0=sQuery(id+"F0.wireOp",EDGE,"0c9ff568-a65c-4a2a-8a0e-bc50d92b607b.28.2.0");var subQ1=sQuery(id+"F0.wireOp",EDGE,"0c9ff568-a65c-4a2a-8a0e-bc50d92b607b.2.2.0");var subQ2=sQuery(id+"F0.wireOp",EDGE,"a8acdf89-7f2b-4dc1-95ab-7df2acf25f29.1.0.2");var subQ3=makeQuery(id+"F0.imprint","INTERSECT",VERTEX,{"disambiguationData":[OD(0.0)],"derivedFrom":[subQ2,subQ1,subQ0]});Q1=makeQuery(id+"F0.imprint","IMPRINT",FACE,{"disambiguationData":[TD([[makeQuery(id+"F0.imprint","IMPRINT",EDGE,{"disambiguationData":[TD([[subQ3,-1.0]])],"derivedFrom":subQ2}),1.0]])]});}
            var Q2;
            {var subQ0=sQuery(id+"F0.wireOp",EDGE,"0c9ff568-a65c-4a2a-8a0e-bc50d92b607b.28.2.0");var subQ1=sQuery(id+"F0.wireOp",EDGE,"0c9ff568-a65c-4a2a-8a0e-bc50d92b607b.2.2.0");var subQ2=sQuery(id+"F0.wireOp",EDGE,"a8acdf89-7f2b-4dc1-95ab-7df2acf25f29.1.0.2");var subQ3=makeQuery(id+"F0.imprint","INTERSECT",VERTEX,{"disambiguationData":[OD(0.0)],"derivedFrom":[subQ2,subQ1,subQ0]});Q2=makeQuery(id+"F0.imprint","IMPRINT",FACE,{"disambiguationData":[TD([[makeQuery(id+"F0.imprint","IMPRINT",EDGE,{"disambiguationData":[TD([[subQ3,1.0]])],"derivedFrom":subQ2}),1.0]])]});}
            var Q3;
            {var subQ0=sQuery(id+"F0.wireOp",EDGE,"0c9ff568-a65c-4a2a-8a0e-bc50d92b607b.28.2.0");var subQ1=sQuery(id+"F0.wireOp",EDGE,"0c9ff568-a65c-4a2a-8a0e-bc50d92b607b.2.2.0");var subQ2=sQuery(id+"F0.wireOp",EDGE,"a8acdf89-7f2b-4dc1-95ab-7df2acf25f29.1.0.2");var subQ3=makeQuery(id+"F0.imprint","INTERSECT",VERTEX,{"disambiguationData":[OD(0.0)],"derivedFrom":[subQ2,subQ1,subQ0]});Q3=makeQuery(id+"F0.imprint","IMPRINT",FACE,{"disambiguationData":[TD([[makeQuery(id+"F0.imprint","IMPRINT",EDGE,{"disambiguationData":[TD([[subQ3,1.0]])],"derivedFrom":subQ2}),-1.0]])]});}
            var Q4;
            {var subQ7=sQuery(id+"F0.wireOp",EDGE,"0c9ff568-a65c-4a2a-8a0e-bc50d92b607b.34.2.0");var subQ9=sQuery(id+"F0.wireOp",EDGE,"0c9ff568-a65c-4a2a-8a0e-bc50d92b607b.0.2.0");var subQ10=makeQuery(id+"F0.imprint","INTERSECT",VERTEX,{"disambiguationData":[OD(0.0)],"derivedFrom":[subQ9,subQ7]});Q4=makeQuery(id+"F0.imprint","IMPRINT",FACE,{"disambiguationData":[TD([[makeQuery(id+"F0.imprint","IMPRINT",EDGE,{"disambiguationData":[TD([[subQ10,1.0]])],"derivedFrom":subQ9}),-1.0]])]});}
            var Q5;
            {var subQ0=sQuery(id+"F0.wireOp",EDGE,"0c9ff568-a65c-4a2a-8a0e-bc50d92b607b.34.2.0");var subQ1=sQuery(id+"F0.wireOp",EDGE,"0c9ff568-a65c-4a2a-8a0e-bc50d92b607b.0.2.0");var subQ2=makeQuery(id+"F0.imprint","INTERSECT",VERTEX,{"disambiguationData":[OD(0.0)],"derivedFrom":[subQ1,subQ0]});Q5=makeQuery(id+"F0.imprint","IMPRINT",FACE,{"disambiguationData":[TD([[makeQuery(id+"F0.imprint","IMPRINT",EDGE,{"disambiguationData":[TD([[subQ2,1.0]])],"derivedFrom":subQ1}),1.0]])]});}
            var Q6;
            {var subQ0=sQuery(id+"F0.wireOp",EDGE,"9e4c2189-47ec-47e2-aa8e-ed7ec2ea7b70.28.3.0");var subQ1=sQuery(id+"F0.wireOp",EDGE,"9e4c2189-47ec-47e2-aa8e-ed7ec2ea7b70.2.3.0");var subQ2=sQuery(id+"F0.wireOp",EDGE,"0c9ff568-a65c-4a2a-8a0e-bc50d92b607b.4.2.0");var subQ3=makeQuery(id+"F0.imprint","INTERSECT",VERTEX,{"disambiguationData":[OD(0.0)],"derivedFrom":[subQ2,subQ1,subQ0]});Q6=makeQuery(id+"F0.imprint","IMPRINT",FACE,{"disambiguationData":[TD([[makeQuery(id+"F0.imprint","IMPRINT",EDGE,{"disambiguationData":[TD([[subQ3,-1.0]])],"derivedFrom":subQ2}),1.0]])]});}
            var Q7;
            {var subQ0=sQuery(id+"F0.wireOp",EDGE,"9e4c2189-47ec-47e2-aa8e-ed7ec2ea7b70.28.3.0");var subQ1=sQuery(id+"F0.wireOp",EDGE,"9e4c2189-47ec-47e2-aa8e-ed7ec2ea7b70.2.3.0");var subQ2=sQuery(id+"F0.wireOp",EDGE,"0c9ff568-a65c-4a2a-8a0e-bc50d92b607b.4.2.0");var subQ3=makeQuery(id+"F0.imprint","INTERSECT",VERTEX,{"disambiguationData":[OD(0.0)],"derivedFrom":[subQ2,subQ1,subQ0]});Q7=makeQuery(id+"F0.imprint","IMPRINT",FACE,{"disambiguationData":[TD([[makeQuery(id+"F0.imprint","IMPRINT",EDGE,{"disambiguationData":[TD([[subQ3,1.0]])],"derivedFrom":subQ2}),1.0]])]});}
            var Q8;
            {var subQ0=sQuery(id+"F0.wireOp",EDGE,"9e4c2189-47ec-47e2-aa8e-ed7ec2ea7b70.28.3.0");var subQ1=sQuery(id+"F0.wireOp",EDGE,"9e4c2189-47ec-47e2-aa8e-ed7ec2ea7b70.2.3.0");var subQ2=sQuery(id+"F0.wireOp",EDGE,"0c9ff568-a65c-4a2a-8a0e-bc50d92b607b.4.2.0");var subQ3=makeQuery(id+"F0.imprint","INTERSECT",VERTEX,{"disambiguationData":[OD(0.0)],"derivedFrom":[subQ2,subQ1,subQ0]});Q8=makeQuery(id+"F0.imprint","IMPRINT",FACE,{"disambiguationData":[TD([[makeQuery(id+"F0.imprint","IMPRINT",EDGE,{"disambiguationData":[TD([[subQ3,1.0]])],"derivedFrom":subQ2}),-1.0]])]});}
            var Q9;
            {var subQ0=sQuery(id+"F0.wireOp",EDGE,"9e4c2189-47ec-47e2-aa8e-ed7ec2ea7b70.28.3.0");var subQ1=sQuery(id+"F0.wireOp",EDGE,"9e4c2189-47ec-47e2-aa8e-ed7ec2ea7b70.2.3.0");var subQ2=sQuery(id+"F0.wireOp",EDGE,"0c9ff568-a65c-4a2a-8a0e-bc50d92b607b.4.2.0");var subQ3=makeQuery(id+"F0.imprint","INTERSECT",VERTEX,{"disambiguationData":[OD(0.0)],"derivedFrom":[subQ2,subQ1,subQ0]});Q9=makeQuery(id+"F0.imprint","IMPRINT",FACE,{"disambiguationData":[TD([[makeQuery(id+"F0.imprint","IMPRINT",EDGE,{"disambiguationData":[TD([[subQ3,-1.0]])],"derivedFrom":subQ1}),1.0]])]});}
            var Q10;
            {var subQ7=sQuery(id+"F0.wireOp",EDGE,"E17.26.0.2");var subQ9=sQuery(id+"F0.wireOp",EDGE,"E17.2.0.2");var subQ16=makeQuery(id+"F0.imprint","INTERSECT",VERTEX,{"disambiguationData":[OD(0.0)],"derivedFrom":[subQ9,subQ7]});Q10=makeQuery(id+"F0.imprint","IMPRINT",FACE,{"disambiguationData":[TD([[makeQuery(id+"F0.imprint","IMPRINT",EDGE,{"disambiguationData":[TD([[subQ16,1.0]])],"derivedFrom":subQ9}),-1.0]])]});}
            var Q11;
            {var subQ0=sQuery(id+"F0.wireOp",EDGE,"E17.29.0.2");var subQ1=sQuery(id+"F0.wireOp",EDGE,"E17.26.0.2");var subQ2=makeQuery(id+"F0.imprint","INTERSECT",VERTEX,{"disambiguationData":[OD(0.0)],"derivedFrom":[subQ1,subQ0]});Q11=makeQuery(id+"F0.imprint","IMPRINT",FACE,{"disambiguationData":[TD([[makeQuery(id+"F0.imprint","IMPRINT",EDGE,{"disambiguationData":[TD([[subQ2,-1.0]])],"derivedFrom":subQ1}),1.0]])]});}
            var Q12;
            {var subQ0=sQuery(id+"F0.wireOp",EDGE,"E17.2.1.2");var subQ1=sQuery(id+"F0.wireOp",EDGE,"E17.6.0.2");var subQ2=makeQuery(id+"F0.imprint","INTERSECT",VERTEX,{"disambiguationData":[OD(0.0)],"derivedFrom":[subQ1,subQ0]});Q12=makeQuery(id+"F0.imprint","IMPRINT",FACE,{"disambiguationData":[TD([[makeQuery(id+"F0.imprint","IMPRINT",EDGE,{"disambiguationData":[TD([[subQ2,-1.0]])],"derivedFrom":subQ1}),1.0]])]});}
            var Q13;
            {var subQ0=sQuery(id+"F0.wireOp",EDGE,"E17.29.1.2");var subQ1=sQuery(id+"F0.wireOp",EDGE,"E17.4.0.2");var subQ2=makeQuery(id+"F0.imprint","INTERSECT",VERTEX,{"disambiguationData":[OD(0.0)],"derivedFrom":[subQ1,subQ0]});Q13=makeQuery(id+"F0.imprint","IMPRINT",FACE,{"disambiguationData":[TD([[makeQuery(id+"F0.imprint","IMPRINT",EDGE,{"disambiguationData":[TD([[subQ2,1.0]])],"derivedFrom":subQ1}),-1.0]])]});}
            var Q14;
            {var subQ0=sQuery(id+"F0.wireOp",EDGE,"E17.29.1.2");var subQ1=sQuery(id+"F0.wireOp",EDGE,"E17.26.1.2");var subQ2=sQuery(id+"F0.wireOp",EDGE,"E17.6.0.2");var subQ3=makeQuery(id+"F0.imprint","INTERSECT",VERTEX,{"disambiguationData":[OD(0.0)],"derivedFrom":[subQ2,subQ1,subQ0]});Q14=makeQuery(id+"F0.imprint","IMPRINT",FACE,{"disambiguationData":[TD([[makeQuery(id+"F0.imprint","IMPRINT",EDGE,{"disambiguationData":[TD([[subQ3,1.0]])],"derivedFrom":subQ2}),1.0]])]});}
            var Q15;
            {var subQ0=sQuery(id+"F0.wireOp",EDGE,"E17.29.1.2");var subQ1=sQuery(id+"F0.wireOp",EDGE,"E17.26.1.2");var subQ2=sQuery(id+"F0.wireOp",EDGE,"E17.6.0.2");var subQ3=makeQuery(id+"F0.imprint","INTERSECT",VERTEX,{"disambiguationData":[OD(0.0)],"derivedFrom":[subQ2,subQ1,subQ0]});Q15=makeQuery(id+"F0.imprint","IMPRINT",FACE,{"disambiguationData":[TD([[makeQuery(id+"F0.imprint","IMPRINT",EDGE,{"disambiguationData":[TD([[subQ3,-1.0]])],"derivedFrom":subQ1}),-1.0]])]});}
            var Q16;
            {var subQ0=sQuery(id+"F0.wireOp",EDGE,"E17.26.0.2");var subQ1=sQuery(id+"F0.wireOp",EDGE,"E17.2.0.2");var subQ2=makeQuery(id+"F0.imprint","INTERSECT",VERTEX,{"disambiguationData":[OD(0.0)],"derivedFrom":[subQ1,subQ0]});Q16=makeQuery(id+"F0.imprint","IMPRINT",FACE,{"disambiguationData":[TD([[makeQuery(id+"F0.imprint","IMPRINT",EDGE,{"disambiguationData":[TD([[subQ2,1.0]])],"derivedFrom":subQ1}),1.0]])]});}
            var Q17;
            {var subQ1=sQuery(id+"F0.wireOp",EDGE,"E17.2.1.2");var subQ5=sQuery(id+"F0.wireOp",EDGE,"E17.6.0.2");var subQ6=makeQuery(id+"F0.imprint","INTERSECT",VERTEX,{"disambiguationData":[OD(0.0)],"derivedFrom":[subQ5,subQ1]});Q17=makeQuery(id+"F0.imprint","IMPRINT",FACE,{"disambiguationData":[TD([[makeQuery(id+"F0.imprint","IMPRINT",EDGE,{"disambiguationData":[TD([[subQ6,-1.0]])],"derivedFrom":subQ5}),-1.0]])]});}
            var Q18;
            {var subQ0=sQuery(id+"F0.wireOp",EDGE,"E17.2.1.2");var subQ1=sQuery(id+"F0.wireOp",EDGE,"E17.6.0.2");var subQ2=makeQuery(id+"F0.imprint","INTERSECT",VERTEX,{"disambiguationData":[OD(0.0)],"derivedFrom":[subQ1,subQ0]});Q18=makeQuery(id+"F0.imprint","IMPRINT",FACE,{"disambiguationData":[TD([[makeQuery(id+"F0.imprint","IMPRINT",EDGE,{"disambiguationData":[TD([[subQ2,-1.0]])],"derivedFrom":subQ0}),1.0]])]});}
            var Q19;
            {var subQ0=sQuery(id+"F0.wireOp",EDGE,"E17.29.1.2");var subQ1=sQuery(id+"F0.wireOp",EDGE,"E17.4.0.2");var subQ2=makeQuery(id+"F0.imprint","INTERSECT",VERTEX,{"disambiguationData":[OD(0.0)],"derivedFrom":[subQ1,subQ0]});Q19=makeQuery(id+"F0.imprint","IMPRINT",FACE,{"disambiguationData":[TD([[makeQuery(id+"F0.imprint","IMPRINT",EDGE,{"disambiguationData":[TD([[subQ2,1.0]])],"derivedFrom":subQ1}),1.0]])]});}
            var Q20;
            {var subQ0=sQuery(id+"F0.wireOp",EDGE,"E17.2.1.2");var subQ1=sQuery(id+"F0.wireOp",EDGE,"E17.6.0.2");var subQ2=makeQuery(id+"F0.imprint","INTERSECT",VERTEX,{"disambiguationData":[OD(0.0)],"derivedFrom":[subQ1,subQ0]});Q20=makeQuery(id+"F0.imprint","IMPRINT",FACE,{"disambiguationData":[TD([[makeQuery(id+"F0.imprint","IMPRINT",EDGE,{"disambiguationData":[TD([[subQ2,1.0]])],"derivedFrom":subQ1}),-1.0]])]});}
            var Q21;
            {var subQ0=sQuery(id+"F0.wireOp",EDGE,"E17.2.1.2");var subQ1=sQuery(id+"F0.wireOp",EDGE,"E17.6.0.2");var subQ2=makeQuery(id+"F0.imprint","INTERSECT",VERTEX,{"disambiguationData":[OD(1.0)],"derivedFrom":[subQ1,subQ0]});Q21=makeQuery(id+"F0.imprint","IMPRINT",FACE,{"disambiguationData":[TD([[makeQuery(id+"F0.imprint","IMPRINT",EDGE,{"disambiguationData":[TD([[subQ2,-1.0]])],"derivedFrom":subQ1}),-1.0]])]});}
            extrude(context, id + "F3", {"entities" : qUnion([Q0, Q1, Q2, Q3, Q4, Q5, Q6, Q7, Q8, Q9, Q10, Q11, Q12, Q13, Q14, Q15, Q16, Q17, Q18, Q19, Q20, Q21]), "depth" : 2.5 * mm});
        }
        {
            var Q0;
            {var subQ0=sQuery(id+"F0.wireOp",EDGE,"a8acdf89-7f2b-4dc1-95ab-7df2acf25f29.1.1.14");var subQ1=sQuery(id+"F0.wireOp",EDGE,"a8acdf89-7f2b-4dc1-95ab-7df2acf25f29.1.1.1");var subQ2=sQuery(id+"F0.wireOp",EDGE,"a8acdf89-7f2b-4dc1-95ab-7df2acf25f29.0.1.2");var subQ3=makeQuery(id+"F0.imprint","INTERSECT",VERTEX,{"disambiguationData":[OD(0.0)],"derivedFrom":[subQ2,subQ1,subQ0]});Q0=makeQuery(id+"F0.imprint","IMPRINT",FACE,{"disambiguationData":[TD([[makeQuery(id+"F0.imprint","IMPRINT",EDGE,{"disambiguationData":[TD([[subQ3,-1.0]])],"derivedFrom":subQ2}),1.0]])]});}
            var Q1;
            {var subQ0=sQuery(id+"F0.wireOp",EDGE,"a8acdf89-7f2b-4dc1-95ab-7df2acf25f29.1.1.14");var subQ1=sQuery(id+"F0.wireOp",EDGE,"a8acdf89-7f2b-4dc1-95ab-7df2acf25f29.1.1.1");var subQ2=sQuery(id+"F0.wireOp",EDGE,"a8acdf89-7f2b-4dc1-95ab-7df2acf25f29.0.1.2");var subQ3=makeQuery(id+"F0.imprint","INTERSECT",VERTEX,{"disambiguationData":[OD(0.0)],"derivedFrom":[subQ2,subQ1,subQ0]});Q1=makeQuery(id+"F0.imprint","IMPRINT",FACE,{"disambiguationData":[TD([[makeQuery(id+"F0.imprint","IMPRINT",EDGE,{"disambiguationData":[TD([[subQ3,-1.0]])],"derivedFrom":subQ1}),1.0]])]});}
            var Q2;
            {var subQ0=sQuery(id+"F0.wireOp",EDGE,"a8acdf89-7f2b-4dc1-95ab-7df2acf25f29.1.1.14");var subQ1=sQuery(id+"F0.wireOp",EDGE,"a8acdf89-7f2b-4dc1-95ab-7df2acf25f29.1.1.1");var subQ2=sQuery(id+"F0.wireOp",EDGE,"a8acdf89-7f2b-4dc1-95ab-7df2acf25f29.0.1.2");var subQ3=makeQuery(id+"F0.imprint","INTERSECT",VERTEX,{"disambiguationData":[OD(0.0)],"derivedFrom":[subQ2,subQ1,subQ0]});Q2=makeQuery(id+"F0.imprint","IMPRINT",FACE,{"disambiguationData":[TD([[makeQuery(id+"F0.imprint","IMPRINT",EDGE,{"disambiguationData":[TD([[subQ3,1.0]])],"derivedFrom":subQ2}),1.0]])]});}
            var Q3;
            {var subQ0=sQuery(id+"F0.wireOp",EDGE,"a8acdf89-7f2b-4dc1-95ab-7df2acf25f29.1.1.14");var subQ1=sQuery(id+"F0.wireOp",EDGE,"a8acdf89-7f2b-4dc1-95ab-7df2acf25f29.1.1.1");var subQ2=sQuery(id+"F0.wireOp",EDGE,"a8acdf89-7f2b-4dc1-95ab-7df2acf25f29.0.1.2");var subQ3=makeQuery(id+"F0.imprint","INTERSECT",VERTEX,{"disambiguationData":[OD(0.0)],"derivedFrom":[subQ2,subQ1,subQ0]});Q3=makeQuery(id+"F0.imprint","IMPRINT",FACE,{"disambiguationData":[TD([[makeQuery(id+"F0.imprint","IMPRINT",EDGE,{"disambiguationData":[TD([[subQ3,1.0]])],"derivedFrom":subQ2}),-1.0]])]});}
            var Q4;
            {var subQ12=sQuery(id+"F0.wireOp",EDGE,"a8acdf89-7f2b-4dc1-95ab-7df2acf25f29.1.1.16");var subQ14=sQuery(id+"F0.wireOp",EDGE,"a8acdf89-7f2b-4dc1-95ab-7df2acf25f29.1.1.0");var subQ15=sQuery(id+"F0.wireOp",EDGE,"a8acdf89-7f2b-4dc1-95ab-7df2acf25f29.1.0.11");var subQ20=makeQuery(id+"F0.imprint","INTERSECT",VERTEX,{"disambiguationData":[OD(0.0)],"derivedFrom":[subQ15,subQ14,subQ12]});Q4=makeQuery(id+"F0.imprint","IMPRINT",FACE,{"disambiguationData":[TD([[makeQuery(id+"F0.imprint","IMPRINT",EDGE,{"disambiguationData":[TD([[subQ20,1.0]])],"derivedFrom":subQ14}),-1.0]])]});}
            var Q5;
            {var subQ0=sQuery(id+"F0.wireOp",EDGE,"a8acdf89-7f2b-4dc1-95ab-7df2acf25f29.2.1.14");var subQ1=sQuery(id+"F0.wireOp",EDGE,"a8acdf89-7f2b-4dc1-95ab-7df2acf25f29.2.1.1");var subQ2=sQuery(id+"F0.wireOp",EDGE,"a8acdf89-7f2b-4dc1-95ab-7df2acf25f29.1.1.2");var subQ3=makeQuery(id+"F0.imprint","INTERSECT",VERTEX,{"disambiguationData":[OD(0.0)],"derivedFrom":[subQ2,subQ1,subQ0]});Q5=makeQuery(id+"F0.imprint","IMPRINT",FACE,{"disambiguationData":[TD([[makeQuery(id+"F0.imprint","IMPRINT",EDGE,{"disambiguationData":[TD([[subQ3,-1.0]])],"derivedFrom":subQ1}),1.0]])]});}
            var Q6;
            {var subQ0=sQuery(id+"F0.wireOp",EDGE,"a8acdf89-7f2b-4dc1-95ab-7df2acf25f29.2.1.14");var subQ1=sQuery(id+"F0.wireOp",EDGE,"a8acdf89-7f2b-4dc1-95ab-7df2acf25f29.2.1.1");var subQ2=sQuery(id+"F0.wireOp",EDGE,"a8acdf89-7f2b-4dc1-95ab-7df2acf25f29.1.1.2");var subQ3=makeQuery(id+"F0.imprint","INTERSECT",VERTEX,{"disambiguationData":[OD(0.0)],"derivedFrom":[subQ2,subQ1,subQ0]});Q6=makeQuery(id+"F0.imprint","IMPRINT",FACE,{"disambiguationData":[TD([[makeQuery(id+"F0.imprint","IMPRINT",EDGE,{"disambiguationData":[TD([[subQ3,1.0]])],"derivedFrom":subQ2}),1.0]])]});}
            var Q7;
            {var subQ0=sQuery(id+"F0.wireOp",EDGE,"a8acdf89-7f2b-4dc1-95ab-7df2acf25f29.2.1.14");var subQ1=sQuery(id+"F0.wireOp",EDGE,"a8acdf89-7f2b-4dc1-95ab-7df2acf25f29.2.1.1");var subQ2=sQuery(id+"F0.wireOp",EDGE,"a8acdf89-7f2b-4dc1-95ab-7df2acf25f29.1.1.2");var subQ3=makeQuery(id+"F0.imprint","INTERSECT",VERTEX,{"disambiguationData":[OD(0.0)],"derivedFrom":[subQ2,subQ1,subQ0]});Q7=makeQuery(id+"F0.imprint","IMPRINT",FACE,{"disambiguationData":[TD([[makeQuery(id+"F0.imprint","IMPRINT",EDGE,{"disambiguationData":[TD([[subQ3,-1.0]])],"derivedFrom":subQ2}),1.0]])]});}
            var Q8;
            {var subQ0=sQuery(id+"F0.wireOp",EDGE,"a8acdf89-7f2b-4dc1-95ab-7df2acf25f29.2.1.14");var subQ1=sQuery(id+"F0.wireOp",EDGE,"a8acdf89-7f2b-4dc1-95ab-7df2acf25f29.2.1.1");var subQ2=sQuery(id+"F0.wireOp",EDGE,"a8acdf89-7f2b-4dc1-95ab-7df2acf25f29.1.1.2");var subQ3=makeQuery(id+"F0.imprint","INTERSECT",VERTEX,{"disambiguationData":[OD(0.0)],"derivedFrom":[subQ2,subQ1,subQ0]});Q8=makeQuery(id+"F0.imprint","IMPRINT",FACE,{"disambiguationData":[TD([[makeQuery(id+"F0.imprint","IMPRINT",EDGE,{"disambiguationData":[TD([[subQ3,1.0]])],"derivedFrom":subQ2}),-1.0]])]});}
            var Q9;
            {var subQ0=sQuery(id+"F0.wireOp",EDGE,"0c9ff568-a65c-4a2a-8a0e-bc50d92b607b.28.2.1");var subQ1=sQuery(id+"F0.wireOp",EDGE,"0c9ff568-a65c-4a2a-8a0e-bc50d92b607b.2.2.1");var subQ2=sQuery(id+"F0.wireOp",EDGE,"a8acdf89-7f2b-4dc1-95ab-7df2acf25f29.1.1.2");var subQ3=makeQuery(id+"F0.imprint","INTERSECT",VERTEX,{"disambiguationData":[OD(0.0)],"derivedFrom":[subQ2,subQ1,subQ0]});Q9=makeQuery(id+"F0.imprint","IMPRINT",FACE,{"disambiguationData":[TD([[makeQuery(id+"F0.imprint","IMPRINT",EDGE,{"disambiguationData":[TD([[subQ3,-1.0]])],"derivedFrom":subQ1}),1.0]])]});}
            var Q10;
            {var subQ0=sQuery(id+"F0.wireOp",EDGE,"E16.1.1.1");var subQ1=sQuery(id+"F0.wireOp",EDGE,"E16.0.1.3");var subQ2=makeQuery(id+"F0.imprint","INTERSECT",VERTEX,{"disambiguationData":[OD(0.0)],"derivedFrom":[subQ1,subQ0]});Q10=makeQuery(id+"F0.imprint","IMPRINT",FACE,{"disambiguationData":[TD([[makeQuery(id+"F0.imprint","IMPRINT",EDGE,{"disambiguationData":[TD([[subQ2,-1.0]])],"derivedFrom":subQ1}),1.0]])]});}
            var Q11;
            {var subQ0=sQuery(id+"F0.wireOp",EDGE,"E16.1.1.6");var subQ20=sQuery(id+"F0.wireOp",EDGE,"E17.36.1.2");var subQ21=sQuery(id+"F0.wireOp",EDGE,"E16.1.1.0");var subQ22=makeQuery(id+"F0.imprint","INTERSECT",VERTEX,{"disambiguationData":[OD(0.0)],"derivedFrom":[subQ21,subQ0,subQ20]});Q11=makeQuery(id+"F0.imprint","IMPRINT",FACE,{"disambiguationData":[TD([[makeQuery(id+"F0.imprint","IMPRINT",EDGE,{"disambiguationData":[TD([[subQ22,1.0]])],"derivedFrom":subQ21}),-1.0]])]});}
            var Q12;
            {var subQ0=sQuery(id+"F0.wireOp",EDGE,"E16.1.1.12");var subQ1=sQuery(id+"F0.wireOp",EDGE,"E16.0.1.2");var subQ2=makeQuery(id+"F0.imprint","INTERSECT",VERTEX,{"disambiguationData":[OD(0.0)],"derivedFrom":[subQ1,subQ0]});Q12=makeQuery(id+"F0.imprint","IMPRINT",FACE,{"disambiguationData":[TD([[makeQuery(id+"F0.imprint","IMPRINT",EDGE,{"disambiguationData":[TD([[subQ2,1.0]])],"derivedFrom":subQ1}),-1.0]])]});}
            var Q13;
            {var subQ0=sQuery(id+"F0.wireOp",EDGE,"E16.1.1.12");var subQ1=sQuery(id+"F0.wireOp",EDGE,"E16.1.1.11");var subQ2=sQuery(id+"F0.wireOp",EDGE,"E16.0.1.3");var subQ3=makeQuery(id+"F0.imprint","INTERSECT",VERTEX,{"disambiguationData":[OD(0.0)],"derivedFrom":[subQ2,subQ1,subQ0]});Q13=makeQuery(id+"F0.imprint","IMPRINT",FACE,{"disambiguationData":[TD([[makeQuery(id+"F0.imprint","IMPRINT",EDGE,{"disambiguationData":[TD([[subQ3,1.0]])],"derivedFrom":subQ2}),1.0]])]});}
            var Q14;
            {var subQ0=sQuery(id+"F0.wireOp",EDGE,"E16.1.1.12");var subQ1=sQuery(id+"F0.wireOp",EDGE,"E16.1.1.11");var subQ2=sQuery(id+"F0.wireOp",EDGE,"E16.0.1.3");var subQ3=makeQuery(id+"F0.imprint","INTERSECT",VERTEX,{"disambiguationData":[OD(0.0)],"derivedFrom":[subQ2,subQ1,subQ0]});Q14=makeQuery(id+"F0.imprint","IMPRINT",FACE,{"disambiguationData":[TD([[makeQuery(id+"F0.imprint","IMPRINT",EDGE,{"disambiguationData":[TD([[subQ3,-1.0]])],"derivedFrom":subQ1}),-1.0]])]});}
            var Q15;
            {var subQ0=sQuery(id+"F0.wireOp",EDGE,"E16.2.1.12");var subQ1=sQuery(id+"F0.wireOp",EDGE,"E16.1.1.2");var subQ2=makeQuery(id+"F0.imprint","INTERSECT",VERTEX,{"disambiguationData":[OD(0.0)],"derivedFrom":[subQ1,subQ0]});Q15=makeQuery(id+"F0.imprint","IMPRINT",FACE,{"disambiguationData":[TD([[makeQuery(id+"F0.imprint","IMPRINT",EDGE,{"disambiguationData":[TD([[subQ2,1.0]])],"derivedFrom":subQ1}),-1.0]])]});}
            var Q16;
            {var subQ0=sQuery(id+"F0.wireOp",EDGE,"E16.2.1.12");var subQ1=sQuery(id+"F0.wireOp",EDGE,"E16.2.1.11");var subQ2=sQuery(id+"F0.wireOp",EDGE,"E16.1.1.3");var subQ3=makeQuery(id+"F0.imprint","INTERSECT",VERTEX,{"disambiguationData":[OD(0.0)],"derivedFrom":[subQ2,subQ1,subQ0]});Q16=makeQuery(id+"F0.imprint","IMPRINT",FACE,{"disambiguationData":[TD([[makeQuery(id+"F0.imprint","IMPRINT",EDGE,{"disambiguationData":[TD([[subQ3,1.0]])],"derivedFrom":subQ2}),1.0]])]});}
            var Q17;
            {var subQ0=sQuery(id+"F0.wireOp",EDGE,"E16.2.1.12");var subQ1=sQuery(id+"F0.wireOp",EDGE,"E16.2.1.11");var subQ2=sQuery(id+"F0.wireOp",EDGE,"E16.1.1.3");var subQ3=makeQuery(id+"F0.imprint","INTERSECT",VERTEX,{"disambiguationData":[OD(0.0)],"derivedFrom":[subQ2,subQ1,subQ0]});Q17=makeQuery(id+"F0.imprint","IMPRINT",FACE,{"disambiguationData":[TD([[makeQuery(id+"F0.imprint","IMPRINT",EDGE,{"disambiguationData":[TD([[subQ3,-1.0]])],"derivedFrom":subQ1}),-1.0]])]});}
            var Q18;
            {var subQ0=sQuery(id+"F0.wireOp",EDGE,"E16.2.1.1");var subQ1=sQuery(id+"F0.wireOp",EDGE,"E16.1.1.3");var subQ2=makeQuery(id+"F0.imprint","INTERSECT",VERTEX,{"disambiguationData":[OD(0.0)],"derivedFrom":[subQ1,subQ0]});Q18=makeQuery(id+"F0.imprint","IMPRINT",FACE,{"disambiguationData":[TD([[makeQuery(id+"F0.imprint","IMPRINT",EDGE,{"disambiguationData":[TD([[subQ2,-1.0]])],"derivedFrom":subQ1}),1.0]])]});}
            var Q19;
            {var subQ0=sQuery(id+"F0.wireOp",EDGE,"E16.1.1.12");var subQ1=sQuery(id+"F0.wireOp",EDGE,"E16.0.1.2");var subQ2=makeQuery(id+"F0.imprint","INTERSECT",VERTEX,{"disambiguationData":[OD(0.0)],"derivedFrom":[subQ1,subQ0]});Q19=makeQuery(id+"F0.imprint","IMPRINT",FACE,{"disambiguationData":[TD([[makeQuery(id+"F0.imprint","IMPRINT",EDGE,{"disambiguationData":[TD([[subQ2,1.0]])],"derivedFrom":subQ1}),1.0]])]});}
            var Q20;
            {var subQ0=sQuery(id+"F0.wireOp",EDGE,"E16.1.1.1");var subQ1=sQuery(id+"F0.wireOp",EDGE,"E16.0.1.3");var subQ2=makeQuery(id+"F0.imprint","INTERSECT",VERTEX,{"disambiguationData":[OD(0.0)],"derivedFrom":[subQ1,subQ0]});Q20=makeQuery(id+"F0.imprint","IMPRINT",FACE,{"disambiguationData":[TD([[makeQuery(id+"F0.imprint","IMPRINT",EDGE,{"disambiguationData":[TD([[subQ2,-1.0]])],"derivedFrom":subQ0}),1.0]])]});}
            var Q21;
            {var subQ0=sQuery(id+"F0.wireOp",EDGE,"E16.1.1.12");var subQ1=sQuery(id+"F0.wireOp",EDGE,"E16.0.1.2");var subQ2=makeQuery(id+"F0.imprint","INTERSECT",VERTEX,{"disambiguationData":[OD(0.0)],"derivedFrom":[subQ1,subQ0]});Q21=makeQuery(id+"F0.imprint","IMPRINT",FACE,{"disambiguationData":[TD([[makeQuery(id+"F0.imprint","IMPRINT",EDGE,{"disambiguationData":[TD([[subQ2,1.0]])],"derivedFrom":subQ0}),-1.0]])]});}
            var Q22;
            {var subQ0=sQuery(id+"F0.wireOp",EDGE,"E16.1.1.12");var subQ1=sQuery(id+"F0.wireOp",EDGE,"E16.0.1.2");var subQ2=makeQuery(id+"F0.imprint","INTERSECT",VERTEX,{"disambiguationData":[OD(0.0)],"derivedFrom":[subQ1,subQ0]});Q22=makeQuery(id+"F0.imprint","IMPRINT",FACE,{"disambiguationData":[TD([[makeQuery(id+"F0.imprint","IMPRINT",EDGE,{"disambiguationData":[TD([[subQ2,-1.0]])],"derivedFrom":subQ1}),1.0]])]});}
            var Q23;
            {var subQ0=sQuery(id+"F0.wireOp",EDGE,"E16.1.1.12");var subQ1=sQuery(id+"F0.wireOp",EDGE,"E16.0.1.2");var subQ2=makeQuery(id+"F0.imprint","INTERSECT",VERTEX,{"disambiguationData":[OD(1.0)],"derivedFrom":[subQ1,subQ0]});Q23=makeQuery(id+"F0.imprint","IMPRINT",FACE,{"disambiguationData":[TD([[makeQuery(id+"F0.imprint","IMPRINT",EDGE,{"disambiguationData":[TD([[subQ2,1.0]])],"derivedFrom":subQ1}),1.0]])]});}
            var Q24;
            {var subQ1=sQuery(id+"F0.wireOp",EDGE,"E16.2.1.1");var subQ5=sQuery(id+"F0.wireOp",EDGE,"E16.1.1.3");var subQ6=makeQuery(id+"F0.imprint","INTERSECT",VERTEX,{"disambiguationData":[OD(0.0)],"derivedFrom":[subQ5,subQ1]});Q24=makeQuery(id+"F0.imprint","IMPRINT",FACE,{"disambiguationData":[TD([[makeQuery(id+"F0.imprint","IMPRINT",EDGE,{"disambiguationData":[TD([[subQ6,-1.0]])],"derivedFrom":subQ5}),-1.0]])]});}
            var Q25;
            {var subQ0=sQuery(id+"F0.wireOp",EDGE,"E16.2.1.1");var subQ1=sQuery(id+"F0.wireOp",EDGE,"E16.1.1.3");var subQ2=makeQuery(id+"F0.imprint","INTERSECT",VERTEX,{"disambiguationData":[OD(1.0)],"derivedFrom":[subQ1,subQ0]});Q25=makeQuery(id+"F0.imprint","IMPRINT",FACE,{"disambiguationData":[TD([[makeQuery(id+"F0.imprint","IMPRINT",EDGE,{"disambiguationData":[TD([[subQ2,-1.0]])],"derivedFrom":subQ1}),-1.0]])]});}
            var Q26;
            {var subQ0=sQuery(id+"F0.wireOp",EDGE,"E16.2.1.1");var subQ1=sQuery(id+"F0.wireOp",EDGE,"E16.1.1.3");var subQ2=makeQuery(id+"F0.imprint","INTERSECT",VERTEX,{"disambiguationData":[OD(0.0)],"derivedFrom":[subQ1,subQ0]});Q26=makeQuery(id+"F0.imprint","IMPRINT",FACE,{"disambiguationData":[TD([[makeQuery(id+"F0.imprint","IMPRINT",EDGE,{"disambiguationData":[TD([[subQ2,-1.0]])],"derivedFrom":subQ0}),1.0]])]});}
            var Q27;
            {var subQ0=sQuery(id+"F0.wireOp",EDGE,"E16.2.1.12");var subQ1=sQuery(id+"F0.wireOp",EDGE,"E16.1.1.2");var subQ2=makeQuery(id+"F0.imprint","INTERSECT",VERTEX,{"disambiguationData":[OD(0.0)],"derivedFrom":[subQ1,subQ0]});Q27=makeQuery(id+"F0.imprint","IMPRINT",FACE,{"disambiguationData":[TD([[makeQuery(id+"F0.imprint","IMPRINT",EDGE,{"disambiguationData":[TD([[subQ2,1.0]])],"derivedFrom":subQ1}),1.0]])]});}
            var Q28;
            {var subQ0=sQuery(id+"F0.wireOp",EDGE,"E16.2.1.1");var subQ1=sQuery(id+"F0.wireOp",EDGE,"E16.1.1.3");var subQ2=makeQuery(id+"F0.imprint","INTERSECT",VERTEX,{"disambiguationData":[OD(0.0)],"derivedFrom":[subQ1,subQ0]});Q28=makeQuery(id+"F0.imprint","IMPRINT",FACE,{"disambiguationData":[TD([[makeQuery(id+"F0.imprint","IMPRINT",EDGE,{"disambiguationData":[TD([[subQ2,1.0]])],"derivedFrom":subQ1}),-1.0]])]});}
            extrude(context, id + "F4", {"entities" : qUnion([Q0, Q1, Q2, Q3, Q4, Q5, Q6, Q7, Q8, Q9, Q10, Q11, Q12, Q13, Q14, Q15, Q16, Q17, Q18, Q19, Q20, Q21, Q22, Q23, Q24, Q25, Q26, Q27, Q28]), "depth" : 2.5 * mm});
        }
        {
            var Q0;
            Q0=makeQuery(id+"F1.opExtrude","SWEPT_BODY",BODY,{"disambiguationData":[OSD([sQuery(id+"F0.wireOp",EDGE,"E0.bottom"),sQuery(id+"F0.wireOp",EDGE,"E0.right"),sQuery(id+"F0.wireOp",EDGE,"E7"),sQuery(id+"F0.wireOp",EDGE,"E0.top"),sQuery(id+"F0.wireOp",EDGE,"E0.left"),sQuery(id+"F0.wireOp",EDGE,"E16.1.0.12")])]});
            var Q1;
            Q1=makeQuery(id+"F2.opExtrude","SWEPT_BODY",BODY,{"disambiguationData":[OSD([sQuery(id+"F0.wireOp",EDGE,"E16.1.0.3"),sQuery(id+"F0.wireOp",EDGE,"E16.2.0.0"),sQuery(id+"F0.wireOp",EDGE,"E16.2.0.2"),sQuery(id+"F0.wireOp",EDGE,"E16.2.0.8"),sQuery(id+"F0.wireOp",EDGE,"E16.2.0.10"),sQuery(id+"F0.wireOp",EDGE,"E16.2.0.11"),sQuery(id+"F0.wireOp",EDGE,"E16.2.1.8")])]});
            var Q2;
            Q2=makeQuery(id+"F4.opExtrude","SWEPT_BODY",BODY,{"disambiguationData":[OSD([sQuery(id+"F0.wireOp",EDGE,"E16.0.1.3"),sQuery(id+"F0.wireOp",EDGE,"E16.1.1.0"),sQuery(id+"F0.wireOp",EDGE,"E16.1.1.8"),sQuery(id+"F0.wireOp",EDGE,"E16.1.1.11"),sQuery(id+"F0.wireOp",EDGE,"E16.1.1.16"),sQuery(id+"F0.wireOp",EDGE,"E16.2.1.11"),sQuery(id+"F0.wireOp",EDGE,"E16.2.1.12"),sQuery(id+"F0.wireOp",EDGE,"E16.1.1.6")])]});
            var Q3;
            Q3=makeQuery(id+"F3.opExtrude","SWEPT_BODY",BODY,{"disambiguationData":[OSD([sQuery(id+"F0.wireOp",EDGE,"E17.0.0.2"),sQuery(id+"F0.wireOp",EDGE,"E16.0.1.6"),sQuery(id+"F0.wireOp",EDGE,"E17.26.0.2"),sQuery(id+"F0.wireOp",EDGE,"E17.36.0.2"),sQuery(id+"F0.wireOp",EDGE,"E17.26.1.2"),sQuery(id+"F0.wireOp",EDGE,"E17.29.1.2"),sQuery(id+"F0.wireOp",EDGE,"f96e19c4-b2ed-4ab6-a718-1c3d16c87367.18.0.3")])]});
            var Q4;
            {var subQ0=sQuery(id+"F0.wireOp",EDGE,"E16.0.1.16");var subQ1=sQuery(id+"F0.wireOp",EDGE,"E0.top");var subQ2=sQuery(id+"F0.wireOp",EDGE,"E7");Q4=makeQuery(id+"F1.opExtrude","SWEPT_EDGE",EDGE,{"disambiguationData":[OSD([subQ2,subQ1,subQ0]),TDD([makeQuery(id+"F0.imprint","INTERSECT",VERTEX,{"disambiguationData":[OD(0.0)],"derivedFrom":[subQ2,subQ1,subQ0]})])]});}
            transform(context, id + "F5", {"entities" : qUnion([Q0, Q1, Q2, Q3]), "transformType" : TransformType.ROTATION, "transformAxis" : qUnion([Q4]), "angle" : 45 * degree, "makeCopy" : false});
        }
        {
            var Q0;
            Q0=makeQuery(id+"F1.opExtrude","CAP_FACE",FACE,{"disambiguationData":[OSD([sQuery(id+"F0.wireOp",EDGE,"E0.bottom"),sQuery(id+"F0.wireOp",EDGE,"E0.right"),sQuery(id+"F0.wireOp",EDGE,"E7"),sQuery(id+"F0.wireOp",EDGE,"E0.top"),sQuery(id+"F0.wireOp",EDGE,"E0.left"),sQuery(id+"F0.wireOp",EDGE,"E16.1.0.12")])],"isStart":false});
            var sketch = newSketch(context, id + "F6", { "sketchPlane" : qUnion([Q0])});
            skLineSegment(sketch, "E19", {"start": v(-54.38, 13.56) * mm, "end": v(-54.38, -71.3) * mm});
            skLineSegment(sketch, "E20", {"start": v(-54.38, -71.3) * mm, "end": v(-49.38, -71.3) * mm});
            skLineSegment(sketch, "E21", {"start": v(-49.38, -71.3) * mm, "end": v(-49.38, 13.56) * mm});
            skLineSegment(sketch, "E22", {"start": v(-49.38, 13.56) * mm, "end": v(-54.38, 13.56) * mm});
            skLineSegment(sketch, "E23.1.0.0", {"start": v(-44.38, -71.3) * mm, "end": v(-44.38, 13.56) * mm});
            skLineSegment(sketch, "E23.1.0.1", {"start": v(-49.38, 13.56) * mm, "end": v(-49.38, -71.3) * mm});
            skLineSegment(sketch, "E23.1.0.2", {"start": v(-44.38, 13.56) * mm, "end": v(-49.38, 13.56) * mm});
            skLineSegment(sketch, "E23.1.0.3", {"start": v(-49.38, -71.3) * mm, "end": v(-44.38, -71.3) * mm});
            skLineSegment(sketch, "E23.2.0.0", {"start": v(-39.38, -71.3) * mm, "end": v(-39.38, 13.56) * mm});
            skLineSegment(sketch, "E23.2.0.1", {"start": v(-44.38, 13.56) * mm, "end": v(-44.38, -71.3) * mm});
            skLineSegment(sketch, "E23.2.0.2", {"start": v(-39.38, 13.56) * mm, "end": v(-44.38, 13.56) * mm});
            skLineSegment(sketch, "E23.2.0.3", {"start": v(-44.38, -71.3) * mm, "end": v(-39.38, -71.3) * mm});
            skLineSegment(sketch, "E23.3.0.0", {"start": v(-34.38, -71.3) * mm, "end": v(-34.38, 13.56) * mm});
            skLineSegment(sketch, "E23.3.0.1", {"start": v(-39.38, 13.56) * mm, "end": v(-39.38, -71.3) * mm});
            skLineSegment(sketch, "E23.3.0.2", {"start": v(-34.38, 13.56) * mm, "end": v(-39.38, 13.56) * mm});
            skLineSegment(sketch, "E23.3.0.3", {"start": v(-39.38, -71.3) * mm, "end": v(-34.38, -71.3) * mm});
            skLineSegment(sketch, "E23.4.0.0", {"start": v(-29.38, -71.3) * mm, "end": v(-29.38, 13.56) * mm});
            skLineSegment(sketch, "E23.4.0.1", {"start": v(-34.38, 13.56) * mm, "end": v(-34.38, -71.3) * mm});
            skLineSegment(sketch, "E23.4.0.2", {"start": v(-29.38, 13.56) * mm, "end": v(-34.38, 13.56) * mm});
            skLineSegment(sketch, "E23.4.0.3", {"start": v(-34.38, -71.3) * mm, "end": v(-29.38, -71.3) * mm});
            skLineSegment(sketch, "E23.5.0.0", {"start": v(-24.38, -71.3) * mm, "end": v(-24.38, 13.56) * mm});
            skLineSegment(sketch, "E23.5.0.1", {"start": v(-29.38, 13.56) * mm, "end": v(-29.38, -71.3) * mm});
            skLineSegment(sketch, "E23.5.0.2", {"start": v(-24.38, 13.56) * mm, "end": v(-29.38, 13.56) * mm});
            skLineSegment(sketch, "E23.5.0.3", {"start": v(-29.38, -71.3) * mm, "end": v(-24.38, -71.3) * mm});
            skLineSegment(sketch, "E23.6.0.0", {"start": v(-19.38, -71.3) * mm, "end": v(-19.38, 13.56) * mm});
            skLineSegment(sketch, "E23.6.0.1", {"start": v(-24.38, 13.56) * mm, "end": v(-24.38, -71.3) * mm});
            skLineSegment(sketch, "E23.6.0.2", {"start": v(-19.38, 13.56) * mm, "end": v(-24.38, 13.56) * mm});
            skLineSegment(sketch, "E23.6.0.3", {"start": v(-24.38, -71.3) * mm, "end": v(-19.38, -71.3) * mm});
            skLineSegment(sketch, "E23.7.0.0", {"start": v(-14.38, -71.3) * mm, "end": v(-14.38, 13.56) * mm});
            skLineSegment(sketch, "E23.7.0.1", {"start": v(-19.38, 13.56) * mm, "end": v(-19.38, -71.3) * mm});
            skLineSegment(sketch, "E23.7.0.2", {"start": v(-14.38, 13.56) * mm, "end": v(-19.38, 13.56) * mm});
            skLineSegment(sketch, "E23.7.0.3", {"start": v(-19.38, -71.3) * mm, "end": v(-14.38, -71.3) * mm});
            skLineSegment(sketch, "E23.8.0.0", {"start": v(-9.38, -71.3) * mm, "end": v(-9.38, 13.56) * mm});
            skLineSegment(sketch, "E23.8.0.1", {"start": v(-14.38, 13.56) * mm, "end": v(-14.38, -71.3) * mm});
            skLineSegment(sketch, "E23.8.0.2", {"start": v(-9.38, 13.56) * mm, "end": v(-14.38, 13.56) * mm});
            skLineSegment(sketch, "E23.8.0.3", {"start": v(-14.38, -71.3) * mm, "end": v(-9.38, -71.3) * mm});
            skLineSegment(sketch, "E23.9.0.0", {"start": v(-4.38, -71.3) * mm, "end": v(-4.38, 13.56) * mm});
            skLineSegment(sketch, "E23.9.0.1", {"start": v(-9.38, 13.56) * mm, "end": v(-9.38, -71.3) * mm});
            skLineSegment(sketch, "E23.9.0.2", {"start": v(-4.38, 13.56) * mm, "end": v(-9.38, 13.56) * mm});
            skLineSegment(sketch, "E23.9.0.3", {"start": v(-9.38, -71.3) * mm, "end": v(-4.38, -71.3) * mm});
            skLineSegment(sketch, "E23.10.0.0", {"start": v(0.62, -71.3) * mm, "end": v(0.62, 13.56) * mm});
            skLineSegment(sketch, "E23.10.0.1", {"start": v(-4.38, 13.56) * mm, "end": v(-4.38, -71.3) * mm});
            skLineSegment(sketch, "E23.10.0.2", {"start": v(0.62, 13.56) * mm, "end": v(-4.38, 13.56) * mm});
            skLineSegment(sketch, "E23.10.0.3", {"start": v(-4.38, -71.3) * mm, "end": v(0.62, -71.3) * mm});
            skLineSegment(sketch, "E23.11.0.0", {"start": v(5.62, -71.3) * mm, "end": v(5.62, 13.56) * mm});
            skLineSegment(sketch, "E23.11.0.1", {"start": v(0.62, 13.56) * mm, "end": v(0.62, -71.3) * mm});
            skLineSegment(sketch, "E23.11.0.2", {"start": v(5.62, 13.56) * mm, "end": v(0.62, 13.56) * mm});
            skLineSegment(sketch, "E23.11.0.3", {"start": v(0.62, -71.3) * mm, "end": v(5.62, -71.3) * mm});
            skLineSegment(sketch, "E23.12.0.0", {"start": v(10.62, -71.3) * mm, "end": v(10.62, 13.56) * mm});
            skLineSegment(sketch, "E23.12.0.1", {"start": v(5.62, 13.56) * mm, "end": v(5.62, -71.3) * mm});
            skLineSegment(sketch, "E23.12.0.2", {"start": v(10.62, 13.56) * mm, "end": v(5.62, 13.56) * mm});
            skLineSegment(sketch, "E23.12.0.3", {"start": v(5.62, -71.3) * mm, "end": v(10.62, -71.3) * mm});
            skLineSegment(sketch, "E23.13.0.0", {"start": v(15.62, -71.3) * mm, "end": v(15.62, 13.56) * mm});
            skLineSegment(sketch, "E23.13.0.1", {"start": v(10.62, 13.56) * mm, "end": v(10.62, -71.3) * mm});
            skLineSegment(sketch, "E23.13.0.2", {"start": v(15.62, 13.56) * mm, "end": v(10.62, 13.56) * mm});
            skLineSegment(sketch, "E23.13.0.3", {"start": v(10.62, -71.3) * mm, "end": v(15.62, -71.3) * mm});
            skLineSegment(sketch, "E23.14.0.0", {"start": v(20.62, -71.3) * mm, "end": v(20.62, 13.56) * mm});
            skLineSegment(sketch, "E23.14.0.1", {"start": v(15.62, 13.56) * mm, "end": v(15.62, -71.3) * mm});
            skLineSegment(sketch, "E23.14.0.2", {"start": v(20.62, 13.56) * mm, "end": v(15.62, 13.56) * mm});
            skLineSegment(sketch, "E23.14.0.3", {"start": v(15.62, -71.3) * mm, "end": v(20.62, -71.3) * mm});
            skLineSegment(sketch, "E23.15.0.0", {"start": v(25.62, -71.3) * mm, "end": v(25.62, 13.56) * mm});
            skLineSegment(sketch, "E23.15.0.1", {"start": v(20.62, 13.56) * mm, "end": v(20.62, -71.3) * mm});
            skLineSegment(sketch, "E23.15.0.2", {"start": v(25.62, 13.56) * mm, "end": v(20.62, 13.56) * mm});
            skLineSegment(sketch, "E23.15.0.3", {"start": v(20.62, -71.3) * mm, "end": v(25.62, -71.3) * mm});
            skLineSegment(sketch, "E23.16.0.0", {"start": v(30.62, -71.3) * mm, "end": v(30.62, 13.56) * mm});
            skLineSegment(sketch, "E23.16.0.1", {"start": v(25.62, 13.56) * mm, "end": v(25.62, -71.3) * mm});
            skLineSegment(sketch, "E23.16.0.2", {"start": v(30.62, 13.56) * mm, "end": v(25.62, 13.56) * mm});
            skLineSegment(sketch, "E23.16.0.3", {"start": v(25.62, -71.3) * mm, "end": v(30.62, -71.3) * mm});
            skLineSegment(sketch, "E23.17.0.0", {"start": v(35.62, -71.3) * mm, "end": v(35.62, 13.56) * mm});
            skLineSegment(sketch, "E23.17.0.1", {"start": v(30.62, 13.56) * mm, "end": v(30.62, -71.3) * mm});
            skLineSegment(sketch, "E23.17.0.2", {"start": v(35.62, 13.56) * mm, "end": v(30.62, 13.56) * mm});
            skLineSegment(sketch, "E23.17.0.3", {"start": v(30.62, -71.3) * mm, "end": v(35.62, -71.3) * mm});
            skLineSegment(sketch, "E23.18.0.0", {"start": v(40.62, -71.3) * mm, "end": v(40.62, 13.56) * mm});
            skLineSegment(sketch, "E23.18.0.1", {"start": v(35.62, 13.56) * mm, "end": v(35.62, -71.3) * mm});
            skLineSegment(sketch, "E23.18.0.2", {"start": v(40.62, 13.56) * mm, "end": v(35.62, 13.56) * mm});
            skLineSegment(sketch, "E23.18.0.3", {"start": v(35.62, -71.3) * mm, "end": v(40.62, -71.3) * mm});
            skLineSegment(sketch, "E23.19.0.0", {"start": v(45.62, -71.3) * mm, "end": v(45.62, 13.56) * mm});
            skLineSegment(sketch, "E23.19.0.1", {"start": v(40.62, 13.56) * mm, "end": v(40.62, -71.3) * mm});
            skLineSegment(sketch, "E23.19.0.2", {"start": v(45.62, 13.56) * mm, "end": v(40.62, 13.56) * mm});
            skLineSegment(sketch, "E23.19.0.3", {"start": v(40.62, -71.3) * mm, "end": v(45.62, -71.3) * mm});
            skLineSegment(sketch, "E23.20.0.0", {"start": v(50.62, -71.3) * mm, "end": v(50.62, 13.56) * mm});
            skLineSegment(sketch, "E23.20.0.1", {"start": v(45.62, 13.56) * mm, "end": v(45.62, -71.3) * mm});
            skLineSegment(sketch, "E23.20.0.2", {"start": v(50.62, 13.56) * mm, "end": v(45.62, 13.56) * mm});
            skLineSegment(sketch, "E23.20.0.3", {"start": v(45.62, -71.3) * mm, "end": v(50.62, -71.3) * mm});
            skLineSegment(sketch, "E23.21.0.0", {"start": v(55.62, -71.3) * mm, "end": v(55.62, 13.56) * mm});
            skLineSegment(sketch, "E23.21.0.1", {"start": v(50.62, 13.56) * mm, "end": v(50.62, -71.3) * mm});
            skLineSegment(sketch, "E23.21.0.2", {"start": v(55.62, 13.56) * mm, "end": v(50.62, 13.56) * mm});
            skLineSegment(sketch, "E23.21.0.3", {"start": v(50.62, -71.3) * mm, "end": v(55.62, -71.3) * mm});
            skLineSegment(sketch, "E23.22.0.0", {"start": v(60.62, -71.3) * mm, "end": v(60.62, 13.56) * mm});
            skLineSegment(sketch, "E23.22.0.1", {"start": v(55.62, 13.56) * mm, "end": v(55.62, -71.3) * mm});
            skLineSegment(sketch, "E23.22.0.2", {"start": v(60.62, 13.56) * mm, "end": v(55.62, 13.56) * mm});
            skLineSegment(sketch, "E23.22.0.3", {"start": v(55.62, -71.3) * mm, "end": v(60.62, -71.3) * mm});
            skLineSegment(sketch, "E23.23.0.0", {"start": v(65.62, -71.3) * mm, "end": v(65.62, 13.56) * mm});
            skLineSegment(sketch, "E23.23.0.1", {"start": v(60.62, 13.56) * mm, "end": v(60.62, -71.3) * mm});
            skLineSegment(sketch, "E23.23.0.2", {"start": v(65.62, 13.56) * mm, "end": v(60.62, 13.56) * mm});
            skLineSegment(sketch, "E23.23.0.3", {"start": v(60.62, -71.3) * mm, "end": v(65.62, -71.3) * mm});
            skLineSegment(sketch, "E23.24.0.0", {"start": v(70.62, -71.3) * mm, "end": v(70.62, 13.56) * mm});
            skLineSegment(sketch, "E23.24.0.1", {"start": v(65.62, 13.56) * mm, "end": v(65.62, -71.3) * mm});
            skLineSegment(sketch, "E23.24.0.2", {"start": v(70.62, 13.56) * mm, "end": v(65.62, 13.56) * mm});
            skLineSegment(sketch, "E23.24.0.3", {"start": v(65.62, -71.3) * mm, "end": v(70.62, -71.3) * mm});
            skLineSegment(sketch, "E23.25.0.0", {"start": v(75.62, -71.3) * mm, "end": v(75.62, 13.56) * mm});
            skLineSegment(sketch, "E23.25.0.1", {"start": v(70.62, 13.56) * mm, "end": v(70.62, -71.3) * mm});
            skLineSegment(sketch, "E23.25.0.2", {"start": v(75.62, 13.56) * mm, "end": v(70.62, 13.56) * mm});
            skLineSegment(sketch, "E23.25.0.3", {"start": v(70.62, -71.3) * mm, "end": v(75.62, -71.3) * mm});
            skLineSegment(sketch, "E23.26.0.0", {"start": v(80.62, -71.3) * mm, "end": v(80.62, 13.56) * mm});
            skLineSegment(sketch, "E23.26.0.1", {"start": v(75.62, 13.56) * mm, "end": v(75.62, -71.3) * mm});
            skLineSegment(sketch, "E23.26.0.2", {"start": v(80.62, 13.56) * mm, "end": v(75.62, 13.56) * mm});
            skLineSegment(sketch, "E23.26.0.3", {"start": v(75.62, -71.3) * mm, "end": v(80.62, -71.3) * mm});
            skLineSegment(sketch, "E23.27.0.0", {"start": v(85.62, -71.3) * mm, "end": v(85.62, 13.56) * mm});
            skLineSegment(sketch, "E23.27.0.1", {"start": v(80.62, 13.56) * mm, "end": v(80.62, -71.3) * mm});
            skLineSegment(sketch, "E23.27.0.2", {"start": v(85.62, 13.56) * mm, "end": v(80.62, 13.56) * mm});
            skLineSegment(sketch, "E23.27.0.3", {"start": v(80.62, -71.3) * mm, "end": v(85.62, -71.3) * mm});
            skLineSegment(sketch, "E23.28.0.0", {"start": v(90.62, -71.3) * mm, "end": v(90.62, 13.56) * mm});
            skLineSegment(sketch, "E23.28.0.1", {"start": v(85.62, 13.56) * mm, "end": v(85.62, -71.3) * mm});
            skLineSegment(sketch, "E23.28.0.2", {"start": v(90.62, 13.56) * mm, "end": v(85.62, 13.56) * mm});
            skLineSegment(sketch, "E23.28.0.3", {"start": v(85.62, -71.3) * mm, "end": v(90.62, -71.3) * mm});
            skLineSegment(sketch, "E23.29.0.0", {"start": v(95.62, -71.3) * mm, "end": v(95.62, 13.56) * mm});
            skLineSegment(sketch, "E23.29.0.1", {"start": v(90.62, 13.56) * mm, "end": v(90.62, -71.3) * mm});
            skLineSegment(sketch, "E23.29.0.2", {"start": v(95.62, 13.56) * mm, "end": v(90.62, 13.56) * mm});
            skLineSegment(sketch, "E23.29.0.3", {"start": v(90.62, -71.3) * mm, "end": v(95.62, -71.3) * mm});
            skLineSegment(sketch, "E23.30.0.0", {"start": v(100.62, -71.3) * mm, "end": v(100.62, 13.56) * mm});
            skLineSegment(sketch, "E23.30.0.1", {"start": v(95.62, 13.56) * mm, "end": v(95.62, -71.3) * mm});
            skLineSegment(sketch, "E23.30.0.2", {"start": v(100.62, 13.56) * mm, "end": v(95.62, 13.56) * mm});
            skLineSegment(sketch, "E23.30.0.3", {"start": v(95.62, -71.3) * mm, "end": v(100.62, -71.3) * mm});
            skLineSegment(sketch, "E23.31.0.0", {"start": v(105.62, -71.3) * mm, "end": v(105.62, 13.56) * mm});
            skLineSegment(sketch, "E23.31.0.1", {"start": v(100.62, 13.56) * mm, "end": v(100.62, -71.3) * mm});
            skLineSegment(sketch, "E23.31.0.2", {"start": v(105.62, 13.56) * mm, "end": v(100.62, 13.56) * mm});
            skLineSegment(sketch, "E23.31.0.3", {"start": v(100.62, -71.3) * mm, "end": v(105.62, -71.3) * mm});
            skLineSegment(sketch, "E23.32.0.0", {"start": v(110.62, -71.3) * mm, "end": v(110.62, 13.56) * mm});
            skLineSegment(sketch, "E23.32.0.1", {"start": v(105.62, 13.56) * mm, "end": v(105.62, -71.3) * mm});
            skLineSegment(sketch, "E23.32.0.2", {"start": v(110.62, 13.56) * mm, "end": v(105.62, 13.56) * mm});
            skLineSegment(sketch, "E23.32.0.3", {"start": v(105.62, -71.3) * mm, "end": v(110.62, -71.3) * mm});
            skLineSegment(sketch, "E23.33.0.0", {"start": v(115.62, -71.3) * mm, "end": v(115.62, 13.56) * mm});
            skLineSegment(sketch, "E23.33.0.1", {"start": v(110.62, 13.56) * mm, "end": v(110.62, -71.3) * mm});
            skLineSegment(sketch, "E23.33.0.2", {"start": v(115.62, 13.56) * mm, "end": v(110.62, 13.56) * mm});
            skLineSegment(sketch, "E23.33.0.3", {"start": v(110.62, -71.3) * mm, "end": v(115.62, -71.3) * mm});
            skLineSegment(sketch, "E23.34.0.0", {"start": v(120.62, -71.3) * mm, "end": v(120.62, 13.56) * mm});
            skLineSegment(sketch, "E23.34.0.1", {"start": v(115.62, 13.56) * mm, "end": v(115.62, -71.3) * mm});
            skLineSegment(sketch, "E23.34.0.2", {"start": v(120.62, 13.56) * mm, "end": v(115.62, 13.56) * mm});
            skLineSegment(sketch, "E23.34.0.3", {"start": v(115.62, -71.3) * mm, "end": v(120.62, -71.3) * mm});
            skLineSegment(sketch, "E23.35.0.0", {"start": v(125.62, -71.3) * mm, "end": v(125.62, 13.56) * mm});
            skLineSegment(sketch, "E23.35.0.1", {"start": v(120.62, 13.56) * mm, "end": v(120.62, -71.3) * mm});
            skLineSegment(sketch, "E23.35.0.2", {"start": v(125.62, 13.56) * mm, "end": v(120.62, 13.56) * mm});
            skLineSegment(sketch, "E23.35.0.3", {"start": v(120.62, -71.3) * mm, "end": v(125.62, -71.3) * mm});
            skLineSegment(sketch, "E23.36.0.0", {"start": v(130.62, -71.3) * mm, "end": v(130.62, 13.56) * mm});
            skLineSegment(sketch, "E23.36.0.1", {"start": v(125.62, 13.56) * mm, "end": v(125.62, -71.3) * mm});
            skLineSegment(sketch, "E23.36.0.2", {"start": v(130.62, 13.56) * mm, "end": v(125.62, 13.56) * mm});
            skLineSegment(sketch, "E23.36.0.3", {"start": v(125.62, -71.3) * mm, "end": v(130.62, -71.3) * mm});
            skLineSegment(sketch, "E23.37.0.0", {"start": v(135.62, -71.3) * mm, "end": v(135.62, 13.56) * mm});
            skLineSegment(sketch, "E23.37.0.1", {"start": v(130.62, 13.56) * mm, "end": v(130.62, -71.3) * mm});
            skLineSegment(sketch, "E23.37.0.2", {"start": v(135.62, 13.56) * mm, "end": v(130.62, 13.56) * mm});
            skLineSegment(sketch, "E23.37.0.3", {"start": v(130.62, -71.3) * mm, "end": v(135.62, -71.3) * mm});
            skLineSegment(sketch, "E23.38.0.0", {"start": v(140.62, -71.3) * mm, "end": v(140.62, 13.56) * mm});
            skLineSegment(sketch, "E23.38.0.1", {"start": v(135.62, 13.56) * mm, "end": v(135.62, -71.3) * mm});
            skLineSegment(sketch, "E23.38.0.2", {"start": v(140.62, 13.56) * mm, "end": v(135.62, 13.56) * mm});
            skLineSegment(sketch, "E23.38.0.3", {"start": v(135.62, -71.3) * mm, "end": v(140.62, -71.3) * mm});
            skLineSegment(sketch, "E23.39.0.0", {"start": v(145.62, -71.3) * mm, "end": v(145.62, 13.56) * mm});
            skLineSegment(sketch, "E23.39.0.1", {"start": v(140.62, 13.56) * mm, "end": v(140.62, -71.3) * mm});
            skLineSegment(sketch, "E23.39.0.2", {"start": v(145.62, 13.56) * mm, "end": v(140.62, 13.56) * mm});
            skLineSegment(sketch, "E23.39.0.3", {"start": v(140.62, -71.3) * mm, "end": v(145.62, -71.3) * mm});
            skLineSegment(sketch, "E23.40.0.0", {"start": v(150.62, -71.3) * mm, "end": v(150.62, 13.56) * mm});
            skLineSegment(sketch, "E23.40.0.1", {"start": v(145.62, 13.56) * mm, "end": v(145.62, -71.3) * mm});
            skLineSegment(sketch, "E23.40.0.2", {"start": v(150.62, 13.56) * mm, "end": v(145.62, 13.56) * mm});
            skLineSegment(sketch, "E23.40.0.3", {"start": v(145.62, -71.3) * mm, "end": v(150.62, -71.3) * mm});
            skLineSegment(sketch, "E23.41.0.0", {"start": v(155.62, -71.3) * mm, "end": v(155.62, 13.56) * mm});
            skLineSegment(sketch, "E23.41.0.1", {"start": v(150.62, 13.56) * mm, "end": v(150.62, -71.3) * mm});
            skLineSegment(sketch, "E23.41.0.2", {"start": v(155.62, 13.56) * mm, "end": v(150.62, 13.56) * mm});
            skLineSegment(sketch, "E23.41.0.3", {"start": v(150.62, -71.3) * mm, "end": v(155.62, -71.3) * mm});
            skLineSegment(sketch, "E23.42.0.0", {"start": v(160.62, -71.3) * mm, "end": v(160.62, 13.56) * mm});
            skLineSegment(sketch, "E23.42.0.1", {"start": v(155.62, 13.56) * mm, "end": v(155.62, -71.3) * mm});
            skLineSegment(sketch, "E23.42.0.2", {"start": v(160.62, 13.56) * mm, "end": v(155.62, 13.56) * mm});
            skLineSegment(sketch, "E23.42.0.3", {"start": v(155.62, -71.3) * mm, "end": v(160.62, -71.3) * mm});
            skLineSegment(sketch, "E23.43.0.0", {"start": v(165.62, -71.3) * mm, "end": v(165.62, 13.56) * mm});
            skLineSegment(sketch, "E23.43.0.1", {"start": v(160.62, 13.56) * mm, "end": v(160.62, -71.3) * mm});
            skLineSegment(sketch, "E23.43.0.2", {"start": v(165.62, 13.56) * mm, "end": v(160.62, 13.56) * mm});
            skLineSegment(sketch, "E23.43.0.3", {"start": v(160.62, -71.3) * mm, "end": v(165.62, -71.3) * mm});
            skLineSegment(sketch, "E23.44.0.0", {"start": v(170.62, -71.3) * mm, "end": v(170.62, 13.56) * mm});
            skLineSegment(sketch, "E23.44.0.1", {"start": v(165.62, 13.56) * mm, "end": v(165.62, -71.3) * mm});
            skLineSegment(sketch, "E23.44.0.2", {"start": v(170.62, 13.56) * mm, "end": v(165.62, 13.56) * mm});
            skLineSegment(sketch, "E23.44.0.3", {"start": v(165.62, -71.3) * mm, "end": v(170.62, -71.3) * mm});
            skLineSegment(sketch, "E23.45.0.0", {"start": v(175.62, -71.3) * mm, "end": v(175.62, 13.56) * mm});
            skLineSegment(sketch, "E23.45.0.1", {"start": v(170.62, 13.56) * mm, "end": v(170.62, -71.3) * mm});
            skLineSegment(sketch, "E23.45.0.2", {"start": v(175.62, 13.56) * mm, "end": v(170.62, 13.56) * mm});
            skLineSegment(sketch, "E23.45.0.3", {"start": v(170.62, -71.3) * mm, "end": v(175.62, -71.3) * mm});
            skLineSegment(sketch, "E23.46.0.0", {"start": v(180.62, -71.3) * mm, "end": v(180.62, 13.56) * mm});
            skLineSegment(sketch, "E23.46.0.1", {"start": v(175.62, 13.56) * mm, "end": v(175.62, -71.3) * mm});
            skLineSegment(sketch, "E23.46.0.2", {"start": v(180.62, 13.56) * mm, "end": v(175.62, 13.56) * mm});
            skLineSegment(sketch, "E23.46.0.3", {"start": v(175.62, -71.3) * mm, "end": v(180.62, -71.3) * mm});
            skLineSegment(sketch, "E23.47.0.0", {"start": v(185.62, -71.3) * mm, "end": v(185.62, 13.56) * mm});
            skLineSegment(sketch, "E23.47.0.1", {"start": v(180.62, 13.56) * mm, "end": v(180.62, -71.3) * mm});
            skLineSegment(sketch, "E23.47.0.2", {"start": v(185.62, 13.56) * mm, "end": v(180.62, 13.56) * mm});
            skLineSegment(sketch, "E23.47.0.3", {"start": v(180.62, -71.3) * mm, "end": v(185.62, -71.3) * mm});
            skLineSegment(sketch, "E23.48.0.0", {"start": v(190.62, -71.3) * mm, "end": v(190.62, 13.56) * mm});
            skLineSegment(sketch, "E23.48.0.1", {"start": v(185.62, 13.56) * mm, "end": v(185.62, -71.3) * mm});
            skLineSegment(sketch, "E23.48.0.2", {"start": v(190.62, 13.56) * mm, "end": v(185.62, 13.56) * mm});
            skLineSegment(sketch, "E23.48.0.3", {"start": v(185.62, -71.3) * mm, "end": v(190.62, -71.3) * mm});
            skLineSegment(sketch, "E23.49.0.0", {"start": v(195.62, -71.3) * mm, "end": v(195.62, 13.56) * mm});
            skLineSegment(sketch, "E23.49.0.1", {"start": v(190.62, 13.56) * mm, "end": v(190.62, -71.3) * mm});
            skLineSegment(sketch, "E23.49.0.2", {"start": v(195.62, 13.56) * mm, "end": v(190.62, 13.56) * mm});
            skLineSegment(sketch, "E23.49.0.3", {"start": v(190.62, -71.3) * mm, "end": v(195.62, -71.3) * mm});
            skLineSegment(sketch, "E23.direction1", {"start": v(-54.38, -71.3) * mm, "end": v(-49.38, -71.3) * mm, "construction": true});
            skPoint(sketch, "E24.0", {"position": v(9.26, 13.56) * mm});
            skPoint(sketch, "E25.0", {"position": v(-33.17, -71.3) * mm});
            skPoint(sketch, "E26.0", {"position": v(-54.38, -50.08) * mm});
            skLineSegment(sketch, "E27.0.50.0", {"start": v(200.62, -71.3) * mm, "end": v(200.62, 13.56) * mm});
            skLineSegment(sketch, "E27.3.50.0", {"start": v(195.62, 13.56) * mm, "end": v(195.62, -71.3) * mm});
            skLineSegment(sketch, "E27.6.50.0", {"start": v(200.62, 13.56) * mm, "end": v(195.62, 13.56) * mm});
            skLineSegment(sketch, "E27.9.50.0", {"start": v(195.62, -71.3) * mm, "end": v(200.62, -71.3) * mm});
            skPoint(sketch, "E28.0", {"position": v(51.68, -71.3) * mm});
            skSolve(sketch);
        }
        {
            var Q0;
            Q0=makeQuery(id+"F1.opExtrude","SWEPT_BODY",BODY,{"disambiguationData":[OSD([sQuery(id+"F0.wireOp",EDGE,"E0.bottom"),sQuery(id+"F0.wireOp",EDGE,"E0.right"),sQuery(id+"F0.wireOp",EDGE,"E7"),sQuery(id+"F0.wireOp",EDGE,"E0.top"),sQuery(id+"F0.wireOp",EDGE,"E0.left"),sQuery(id+"F0.wireOp",EDGE,"E16.1.0.12")])]});
            var Q1;
            Q1=makeQuery(id+"F2.opExtrude","SWEPT_BODY",BODY,{"disambiguationData":[OSD([sQuery(id+"F0.wireOp",EDGE,"E16.1.0.3"),sQuery(id+"F0.wireOp",EDGE,"E16.2.0.0"),sQuery(id+"F0.wireOp",EDGE,"E16.2.0.8"),sQuery(id+"F0.wireOp",EDGE,"E16.2.0.11"),sQuery(id+"F0.wireOp",EDGE,"E16.2.1.8"),sQuery(id+"F0.wireOp",EDGE,"E16.2.0.10"),sQuery(id+"F0.wireOp",EDGE,"E18.29.3.0")])]});
            var Q2;
            Q2=makeQuery(id+"F3.opExtrude","SWEPT_BODY",BODY,{"disambiguationData":[OSD([sQuery(id+"F0.wireOp",EDGE,"E17.0.0.2"),sQuery(id+"F0.wireOp",EDGE,"E17.12.0.2"),sQuery(id+"F0.wireOp",EDGE,"E16.0.1.6"),sQuery(id+"F0.wireOp",EDGE,"E17.26.0.2"),sQuery(id+"F0.wireOp",EDGE,"E17.36.0.2"),sQuery(id+"F0.wireOp",EDGE,"E17.26.1.2"),sQuery(id+"F0.wireOp",EDGE,"E17.29.1.2")])]});
            var Q3;
            Q3=makeQuery(id+"F4.opExtrude","SWEPT_BODY",BODY,{"disambiguationData":[OSD([sQuery(id+"F0.wireOp",EDGE,"E16.0.1.3"),sQuery(id+"F0.wireOp",EDGE,"E16.1.1.0"),sQuery(id+"F0.wireOp",EDGE,"E16.1.1.8"),sQuery(id+"F0.wireOp",EDGE,"E16.1.1.11"),sQuery(id+"F0.wireOp",EDGE,"E16.1.1.16"),sQuery(id+"F0.wireOp",EDGE,"E16.2.1.11"),sQuery(id+"F0.wireOp",EDGE,"E16.2.1.12"),sQuery(id+"F0.wireOp",EDGE,"E16.1.1.6")])]});
            var Q4;
            {var subQ0=sQuery(id+"F0.wireOp",EDGE,"E16.0.1.16");var subQ1=sQuery(id+"F0.wireOp",EDGE,"E0.top");var subQ2=sQuery(id+"F0.wireOp",EDGE,"E7");Q4=makeQuery(id+"F1.opExtrude","SWEPT_EDGE",EDGE,{"disambiguationData":[OSD([subQ2,subQ1,subQ0]),TDD([makeQuery(id+"F0.imprint","INTERSECT",VERTEX,{"disambiguationData":[OD(0.0)],"derivedFrom":[subQ2,subQ1,subQ0]})])]});}
            transform(context, id + "F7", {"entities" : qUnion([Q0, Q1, Q2, Q3]), "transformType" : TransformType.ROTATION, "transformAxis" : qUnion([Q4]), "angle" : 45 * degree, "oppositeDirection" : true, "makeCopy" : false});
        }
    });
